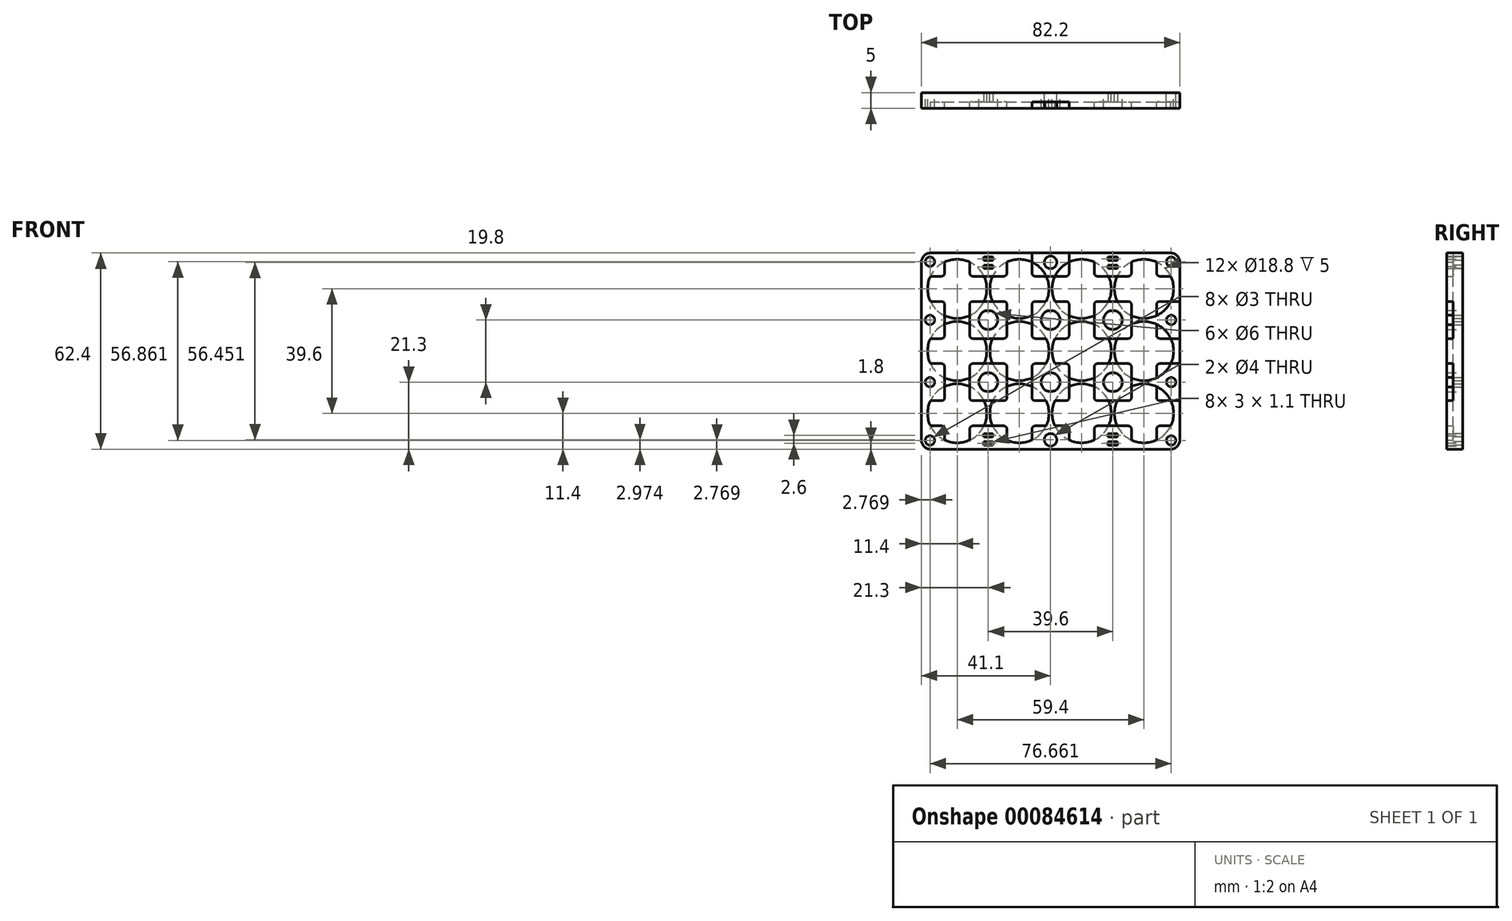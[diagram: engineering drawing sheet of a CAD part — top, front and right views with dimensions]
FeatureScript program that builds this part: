
annotation { "Feature Type Name" : "Feature", "Feature Type Description" : "" }
export const myFeature = defineFeature(function(context is Context, id is Id, definition is map)
    precondition{}
    {
        {
            var Q0;
            Q0=qCreatedBy(makeId("Front.planeOp"),FACE);
            var sketch = newSketch(context, id + "F0", { "sketchPlane" : qUnion([Q0]) });
            skCircle(sketch, "E0", {"center": v(0, 0) * mm, "radius": 9.4 * mm});
            skCircle(sketch, "E1.0.1.0", {"center": v(0, 19.8) * mm, "radius": 9.4 * mm});
            skCircle(sketch, "E1.0.2.0", {"center": v(0, 39.6) * mm, "radius": 9.4 * mm});
            skCircle(sketch, "E1.1.0.0", {"center": v(19.8, 0) * mm, "radius": 9.4 * mm});
            skCircle(sketch, "E1.1.1.0", {"center": v(19.8, 19.8) * mm, "radius": 9.4 * mm});
            skCircle(sketch, "E1.1.2.0", {"center": v(19.8, 39.6) * mm, "radius": 9.4 * mm});
            skCircle(sketch, "E1.2.0.0", {"center": v(39.6, 0) * mm, "radius": 9.4 * mm});
            skCircle(sketch, "E1.2.1.0", {"center": v(39.6, 19.8) * mm, "radius": 9.4 * mm});
            skCircle(sketch, "E1.2.2.0", {"center": v(39.6, 39.6) * mm, "radius": 9.4 * mm});
            skCircle(sketch, "E1.3.0.0", {"center": v(59.4, 0) * mm, "radius": 9.4 * mm});
            skCircle(sketch, "E1.3.1.0", {"center": v(59.4, 19.8) * mm, "radius": 9.4 * mm});
            skCircle(sketch, "E1.3.2.0", {"center": v(59.4, 39.6) * mm, "radius": 9.4 * mm});
            skLineSegment(sketch, "E1.direction1", {"start": v(0, 0) * mm, "end": v(19.8, 0) * mm, "construction": true});
            skLineSegment(sketch, "E1.direction2", {"start": v(0, 0) * mm, "end": v(0, 19.8) * mm, "construction": true});
            skLineSegment(sketch, "E2", {"start": v(-9.4, 19.8) * mm, "end": v(68.8, 19.8) * mm, "construction": true});
            skLineSegment(sketch, "E3", {"start": v(29.7, 19.8) * mm, "end": v(29.7, -16.3) * mm, "construction": true});
            skLineSegment(sketch, "E4.bottom", {"start": v(70.8, -11.4) * mm, "end": v(-11.4, -11.4) * mm});
            skLineSegment(sketch, "E4.top", {"start": v(70.8, 51) * mm, "end": v(-11.4, 51) * mm});
            skLineSegment(sketch, "E4.left", {"start": v(70.8, -11.4) * mm, "end": v(70.8, 51) * mm});
            skLineSegment(sketch, "E4.right", {"start": v(-11.4, -11.4) * mm, "end": v(-11.4, 51) * mm});
            skPoint(sketch, "E4.middle", {"position": v(29.7, 19.8) * mm});
            skLineSegment(sketch, "E5", {"start": v(19.8, 19.8) * mm, "end": v(0, 0) * mm, "construction": true});
            skLineSegment(sketch, "E6", {"start": v(19.8, 0) * mm, "end": v(0, 19.8) * mm, "construction": true});
            skCircle(sketch, "E7", {"center": v(9.9, 9.9) * mm, "radius": 3 * mm});
            skCircle(sketch, "E8.0.1.0", {"center": v(9.9, 29.7) * mm, "radius": 3 * mm});
            skCircle(sketch, "E8.1.0.0", {"center": v(29.7, 9.9) * mm, "radius": 3 * mm});
            skCircle(sketch, "E8.1.1.0", {"center": v(29.7, 29.7) * mm, "radius": 3 * mm});
            skCircle(sketch, "E8.2.0.0", {"center": v(49.5, 9.9) * mm, "radius": 3 * mm});
            skCircle(sketch, "E8.2.1.0", {"center": v(49.5, 29.7) * mm, "radius": 3 * mm});
            skLineSegment(sketch, "E8.direction1", {"start": v(9.9, 9.9) * mm, "end": v(29.7, 9.9) * mm, "construction": true});
            skLineSegment(sketch, "E8.direction2", {"start": v(9.9, 9.9) * mm, "end": v(9.9, 29.7) * mm, "construction": true});
            skLineSegment(sketch, "E9", {"start": v(9.9, 0) * mm, "end": v(9.9, -11.4) * mm, "construction": true});
            skCircle(sketch, "E10.1.0.0", {"center": v(29.7, -8.43) * mm, "radius": 2 * mm});
            skLineSegment(sketch, "E10.direction1", {"start": v(9.9, -8.43) * mm, "end": v(29.7, -8.43) * mm, "construction": true});
            skCircle(sketch, "E11.MirrorC", {"center": v(29.7, 48.03) * mm, "radius": 2 * mm});
            skLineSegment(sketch, "E12", {"start": v(0, 0) * mm, "end": v(-11.4, -11.4) * mm, "construction": true});
            skCircle(sketch, "E13", {"center": v(-8.63, -8.63) * mm, "radius": 1.5 * mm});
            skCircle(sketch, "E14", {"center": v(-8.63, 9.9) * mm, "radius": 1.5 * mm});
            skCircle(sketch, "E15", {"center": v(-8.63, 29.7) * mm, "radius": 1.5 * mm});
            skCircle(sketch, "E16.MirrorC", {"center": v(-8.63, 48.23) * mm, "radius": 1.5 * mm});
            skCircle(sketch, "E17.MirrorC", {"center": v(68.03, -8.63) * mm, "radius": 1.5 * mm});
            skCircle(sketch, "E18.MirrorC", {"center": v(68.03, 9.9) * mm, "radius": 1.5 * mm});
            skCircle(sketch, "E19.MirrorC", {"center": v(68.03, 29.7) * mm, "radius": 1.5 * mm});
            skCircle(sketch, "E20.MirrorC", {"center": v(68.03, 48.23) * mm, "radius": 1.5 * mm});
            skSolve(sketch);
        }
        {
            var Q0;
            Q0=qSketchRegion(id+"F0",true);
            extrude(context, id + "F1", {"entities" : qUnion([Q0]), "depth" : 3 * mm});
        }
        {
            var Q0;
            Q0=makeQuery(id+"F1.opExtrude","SWEPT_EDGE",EDGE,{"disambiguationData":[OSD([sQuery(id+"F0.wireOp",EDGE,"E4.top"),sQuery(id+"F0.wireOp",EDGE,"E4.left")])]});
            var Q1;
            Q1=makeQuery(id+"F1.opExtrude","SWEPT_EDGE",EDGE,{"disambiguationData":[OSD([sQuery(id+"F0.wireOp",EDGE,"E4.top"),sQuery(id+"F0.wireOp",EDGE,"E4.right")])]});
            var Q2;
            Q2=makeQuery(id+"F1.opExtrude","SWEPT_EDGE",EDGE,{"disambiguationData":[OSD([sQuery(id+"F0.wireOp",EDGE,"E4.bottom"),sQuery(id+"F0.wireOp",EDGE,"E4.right")])]});
            var Q3;
            Q3=makeQuery(id+"F1.opExtrude","SWEPT_EDGE",EDGE,{"disambiguationData":[OSD([sQuery(id+"F0.wireOp",EDGE,"E4.bottom"),sQuery(id+"F0.wireOp",EDGE,"E4.left")])]});
            fillet(context, id + "F2", {"entities" : qUnion([Q0, Q1, Q2, Q3]), "radius" : 3 * mm, "tangentPropagation" : true, "conicFillet" : false});
        }
        {
            var Q0;
            Q0=makeQuery(id+"F1.opExtrude","CAP_FACE",FACE,{"disambiguationData":[OSD([sQuery(id+"F0.wireOp",EDGE,"E0"),sQuery(id+"F0.wireOp",EDGE,"E1.0.1.0"),sQuery(id+"F0.wireOp",EDGE,"E1.0.2.0"),sQuery(id+"F0.wireOp",EDGE,"E1.1.0.0"),sQuery(id+"F0.wireOp",EDGE,"E1.1.1.0"),sQuery(id+"F0.wireOp",EDGE,"E1.1.2.0"),sQuery(id+"F0.wireOp",EDGE,"E1.2.0.0"),sQuery(id+"F0.wireOp",EDGE,"E1.2.1.0"),sQuery(id+"F0.wireOp",EDGE,"E1.2.2.0"),sQuery(id+"F0.wireOp",EDGE,"E1.3.0.0"),sQuery(id+"F0.wireOp",EDGE,"E1.3.1.0"),sQuery(id+"F0.wireOp",EDGE,"E1.3.2.0"),sQuery(id+"F0.wireOp",EDGE,"E4.bottom"),sQuery(id+"F0.wireOp",EDGE,"E4.top"),sQuery(id+"F0.wireOp",EDGE,"E4.left"),sQuery(id+"F0.wireOp",EDGE,"E4.right"),sQuery(id+"F0.wireOp",EDGE,"E7"),sQuery(id+"F0.wireOp",EDGE,"E8.0.1.0"),sQuery(id+"F0.wireOp",EDGE,"E8.1.0.0"),sQuery(id+"F0.wireOp",EDGE,"E8.1.1.0"),sQuery(id+"F0.wireOp",EDGE,"E8.2.0.0"),sQuery(id+"F0.wireOp",EDGE,"E8.2.1.0"),sQuery(id+"F0.wireOp",EDGE,"EQu0VpH5-7skk-RFPN-a941-U7lPeWaJFOTF"),sQuery(id+"F0.wireOp",EDGE,"E10.1.0.0"),sQuery(id+"F0.wireOp",EDGE,"E10.2.0.0"),sQuery(id+"F0.wireOp",EDGE,"d1583e0b-7ce3-4cbd-bf89-e67b3cb1275a0.MirrorC"),sQuery(id+"F0.wireOp",EDGE,"E11.MirrorC"),sQuery(id+"F0.wireOp",EDGE,"091dc890-a7a3-4dd7-b955-14caaaf945470.MirrorC"),sQuery(id+"F0.wireOp",EDGE,"E13"),sQuery(id+"F0.wireOp",EDGE,"E14"),sQuery(id+"F0.wireOp",EDGE,"E15"),sQuery(id+"F0.wireOp",EDGE,"E16.MirrorC"),sQuery(id+"F0.wireOp",EDGE,"E17.MirrorC"),sQuery(id+"F0.wireOp",EDGE,"E18.MirrorC"),sQuery(id+"F0.wireOp",EDGE,"E19.MirrorC"),sQuery(id+"F0.wireOp",EDGE,"E20.MirrorC")])],"isStart":false});
            var sketch = newSketch(context, id + "F3", { "sketchPlane" : qUnion([Q0]) });
            skLineSegment(sketch, "E21.0", {"start": v(67.8, 51) * mm, "end": v(-8.4, 51) * mm});
            skArc(sketch, "E21.1", {"start": v(-8.4, 51) * mm, "mid": v(-10.52, 50.12) * mm, "end": v(-11.4, 48) * mm});
            skLineSegment(sketch, "E21.2", {"start": v(-11.4, -8.4) * mm, "end": v(-11.4, 35.6) * mm});
            skArc(sketch, "E21.3", {"start": v(-11.4, -8.4) * mm, "mid": v(-10.52, -10.52) * mm, "end": v(-8.4, -11.4) * mm});
            skLineSegment(sketch, "E21.4", {"start": v(67.8, -11.4) * mm, "end": v(-8.4, -11.4) * mm});
            skArc(sketch, "E21.5", {"start": v(67.8, -11.4) * mm, "mid": v(69.92, -10.52) * mm, "end": v(70.8, -8.4) * mm});
            skLineSegment(sketch, "E21.6", {"start": v(70.8, -8.4) * mm, "end": v(70.8, 48) * mm});
            skArc(sketch, "E21.7", {"start": v(70.8, 48) * mm, "mid": v(69.92, 50.12) * mm, "end": v(67.8, 51) * mm});
            skCircle(sketch, "E21.8", {"center": v(59.4, 39.6) * mm, "radius": 9.4 * mm});
            skCircle(sketch, "E21.9", {"center": v(39.6, 39.6) * mm, "radius": 9.4 * mm});
            skCircle(sketch, "E21.10", {"center": v(19.8, 39.6) * mm, "radius": 9.4 * mm});
            skArc(sketch, "E21.11", {"start": v(-8.5, 43.6) * mm, "mid": v(-9.4, 39.6) * mm, "end": v(-8.5, 35.6) * mm});
            skCircle(sketch, "E21.12", {"center": v(0, 19.8) * mm, "radius": 9.4 * mm});
            skCircle(sketch, "E21.13", {"center": v(19.8, 19.8) * mm, "radius": 9.4 * mm});
            skCircle(sketch, "E21.14", {"center": v(39.6, 19.8) * mm, "radius": 9.4 * mm});
            skCircle(sketch, "E21.15", {"center": v(59.4, 19.8) * mm, "radius": 9.4 * mm});
            skCircle(sketch, "E21.16", {"center": v(59.4, 0) * mm, "radius": 9.4 * mm});
            skCircle(sketch, "E21.17", {"center": v(39.6, 0) * mm, "radius": 9.4 * mm});
            skCircle(sketch, "E21.18", {"center": v(19.8, 0) * mm, "radius": 9.4 * mm});
            skCircle(sketch, "E21.19", {"center": v(0, 0) * mm, "radius": 9.4 * mm});
            skLineSegment(sketch, "E22.left", {"start": v(-11.4, 39.6) * mm, "end": v(-11.4, 43.6) * mm});
            skLineSegment(sketch, "E22.right", {"start": v(70.8, 39.6) * mm, "end": v(70.8, 43.6) * mm});
            skLineSegment(sketch, "E23.trimOffspring", {"start": v(-11.4, 43.6) * mm, "end": v(-11.4, 48) * mm});
            skLineSegment(sketch, "E24", {"start": v(-4, 51) * mm, "end": v(-4, 43.6) * mm});
            skLineSegment(sketch, "E25.MirrorCS", {"start": v(4, 51) * mm, "end": v(4, 43.6) * mm});
            skLineSegment(sketch, "E26", {"start": v(-11.4, -4) * mm, "end": v(-4, -4) * mm});
            skLineSegment(sketch, "E27.MirrorCS", {"start": v(-11.4, 4) * mm, "end": v(-4, 4) * mm});
            skLineSegment(sketch, "E28.1.0.0", {"start": v(15.8, 51) * mm, "end": v(15.8, 43.6) * mm});
            skLineSegment(sketch, "E28.1.0.1", {"start": v(23.8, 51) * mm, "end": v(23.8, 43.6) * mm});
            skLineSegment(sketch, "E28.2.0.0", {"start": v(35.6, 51) * mm, "end": v(35.6, 43.6) * mm});
            skLineSegment(sketch, "E28.2.0.1", {"start": v(43.6, 51) * mm, "end": v(43.6, 43.6) * mm});
            skLineSegment(sketch, "E28.3.0.0", {"start": v(55.4, 51) * mm, "end": v(55.4, 43.6) * mm});
            skLineSegment(sketch, "E28.3.0.1", {"start": v(63.4, 51) * mm, "end": v(63.4, 43.6) * mm});
            skLineSegment(sketch, "E28.direction1", {"start": v(-4, -11.4) * mm, "end": v(15.8, -11.4) * mm, "construction": true});
            skLineSegment(sketch, "E29.0.1.0", {"start": v(-11.4, 23.8) * mm, "end": v(-4, 23.8) * mm});
            skLineSegment(sketch, "E29.0.1.1", {"start": v(-11.4, 15.8) * mm, "end": v(-4, 15.8) * mm});
            skLineSegment(sketch, "E29.0.2.0", {"start": v(-11.4, 43.6) * mm, "end": v(-4, 43.6) * mm});
            skLineSegment(sketch, "E29.0.2.1", {"start": v(-11.4, 35.6) * mm, "end": v(-4, 35.6) * mm});
            skLineSegment(sketch, "E29.direction1", {"start": v(-11.4, 4) * mm, "end": v(-4, 4) * mm, "construction": true});
            skLineSegment(sketch, "E29.direction2", {"start": v(-11.4, 4) * mm, "end": v(-11.4, 23.8) * mm, "construction": true});
            skLineSegment(sketch, "E30.trimOffspring", {"start": v(4, 35.6) * mm, "end": v(15.8, 35.6) * mm});
            skLineSegment(sketch, "E31.trimOffspring", {"start": v(4, 43.6) * mm, "end": v(15.8, 43.6) * mm});
            skLineSegment(sketch, "E32.trimOffspring", {"start": v(4, 35.6) * mm, "end": v(4, 23.8) * mm});
            skLineSegment(sketch, "E33.trimOffspring", {"start": v(-4, 35.6) * mm, "end": v(-4, 23.8) * mm});
            skLineSegment(sketch, "E34.trimOffspring", {"start": v(15.8, 35.6) * mm, "end": v(15.8, 23.8) * mm});
            skLineSegment(sketch, "E35.trimOffspring", {"start": v(23.8, 35.6) * mm, "end": v(23.8, 23.8) * mm});
            skLineSegment(sketch, "E36.trimOffspring", {"start": v(35.6, 35.6) * mm, "end": v(35.6, 23.8) * mm});
            skLineSegment(sketch, "E37.trimOffspring", {"start": v(43.6, 35.6) * mm, "end": v(43.6, 23.8) * mm});
            skLineSegment(sketch, "E38.trimOffspring", {"start": v(55.4, 35.6) * mm, "end": v(55.4, 23.8) * mm});
            skLineSegment(sketch, "E39.trimOffspring", {"start": v(63.4, 35.6) * mm, "end": v(63.4, 23.8) * mm});
            skLineSegment(sketch, "E40.trimOffspring", {"start": v(23.8, 43.6) * mm, "end": v(35.6, 43.6) * mm});
            skLineSegment(sketch, "E41.trimOffspring", {"start": v(43.6, 43.6) * mm, "end": v(55.4, 43.6) * mm});
            skLineSegment(sketch, "E42.trimOffspring", {"start": v(63.4, 43.6) * mm, "end": v(70.8, 43.6) * mm});
            skLineSegment(sketch, "E43.trimOffspring", {"start": v(63.4, 35.6) * mm, "end": v(70.8, 35.6) * mm});
            skLineSegment(sketch, "E44.trimOffspring", {"start": v(43.6, 35.6) * mm, "end": v(55.4, 35.6) * mm});
            skLineSegment(sketch, "E45.trimOffspring", {"start": v(23.8, 35.6) * mm, "end": v(35.6, 35.6) * mm});
            skLineSegment(sketch, "E46.trimOffspring", {"start": v(4, 23.8) * mm, "end": v(15.8, 23.8) * mm});
            skLineSegment(sketch, "E47.trimOffspring", {"start": v(4, 15.8) * mm, "end": v(11.3, 15.8) * mm});
            skLineSegment(sketch, "E48.trimOffspring", {"start": v(-4, 15.8) * mm, "end": v(-4, 4) * mm});
            skLineSegment(sketch, "E49.trimOffspring", {"start": v(4, 15.8) * mm, "end": v(4, 4) * mm});
            skLineSegment(sketch, "E50.trimOffspring", {"start": v(15.8, 15.8) * mm, "end": v(15.8, 4) * mm});
            skLineSegment(sketch, "E51.trimOffspring", {"start": v(23.8, 15.8) * mm, "end": v(23.8, 4) * mm});
            skLineSegment(sketch, "E52.trimOffspring", {"start": v(35.6, 15.8) * mm, "end": v(35.6, 4) * mm});
            skLineSegment(sketch, "E53.trimOffspring", {"start": v(43.6, 15.8) * mm, "end": v(43.6, 4) * mm});
            skLineSegment(sketch, "E54.trimOffspring", {"start": v(55.4, 15.8) * mm, "end": v(55.4, 4) * mm});
            skLineSegment(sketch, "E55.trimOffspring", {"start": v(63.4, 15.8) * mm, "end": v(63.4, 4) * mm});
            skLineSegment(sketch, "E56.trimOffspring", {"start": v(23.8, 23.8) * mm, "end": v(35.6, 23.8) * mm});
            skLineSegment(sketch, "E57.trimOffspring", {"start": v(43.6, 23.8) * mm, "end": v(55.4, 23.8) * mm});
            skLineSegment(sketch, "E58.trimOffspring", {"start": v(63.4, 23.8) * mm, "end": v(70.8, 23.8) * mm});
            skLineSegment(sketch, "E59.trimOffspring", {"start": v(23.8, 15.8) * mm, "end": v(35.6, 15.8) * mm});
            skLineSegment(sketch, "E60.trimOffspring", {"start": v(63.4, 15.8) * mm, "end": v(70.8, 15.8) * mm});
            skLineSegment(sketch, "E61.trimOffspring", {"start": v(63.4, 4) * mm, "end": v(70.8, 4) * mm});
            skLineSegment(sketch, "E62.trimOffspring", {"start": v(43.6, 4) * mm, "end": v(55.4, 4) * mm});
            skLineSegment(sketch, "E63.trimOffspring", {"start": v(23.8, 4) * mm, "end": v(35.6, 4) * mm});
            skLineSegment(sketch, "E64.trimOffspring", {"start": v(4, 4) * mm, "end": v(15.8, 4) * mm});
            skLineSegment(sketch, "E65.trimOffspring", {"start": v(4, -4) * mm, "end": v(11.3, -4) * mm});
            skLineSegment(sketch, "E66.trimOffspring", {"start": v(23.8, -4) * mm, "end": v(35.6, -4) * mm});
            skLineSegment(sketch, "E67.trimOffspring", {"start": v(63.4, -4) * mm, "end": v(70.8, -4) * mm});
            skLineSegment(sketch, "E68.trimOffspring", {"start": v(55.4, -4) * mm, "end": v(55.4, -11.4) * mm});
            skLineSegment(sketch, "E69.trimOffspring", {"start": v(63.4, -4) * mm, "end": v(63.4, -11.4) * mm});
            skLineSegment(sketch, "E70.trimOffspring", {"start": v(43.6, -4) * mm, "end": v(43.6, -11.4) * mm});
            skLineSegment(sketch, "E71.trimOffspring", {"start": v(35.6, -4) * mm, "end": v(35.6, -11.4) * mm});
            skLineSegment(sketch, "E72.trimOffspring", {"start": v(23.8, -4) * mm, "end": v(23.8, -11.4) * mm});
            skLineSegment(sketch, "E73.trimOffspring", {"start": v(4, -4) * mm, "end": v(4, -11.4) * mm});
            skLineSegment(sketch, "E74.trimOffspring", {"start": v(-4, -4) * mm, "end": v(-4, -11.4) * mm});
            skLineSegment(sketch, "E75", {"start": v(11.3, 15.8) * mm, "end": v(15.8, 15.8) * mm});
            skLineSegment(sketch, "E76", {"start": v(11.3, -4) * mm, "end": v(15.8, -4) * mm});
            skLineSegment(sketch, "E77.trimOffspring", {"start": v(15.8, -4) * mm, "end": v(15.8, -11.4) * mm});
            skLineSegment(sketch, "E78.trimOffspring", {"start": v(43.6, 15.8) * mm, "end": v(55.4, 15.8) * mm});
            skLineSegment(sketch, "E79.trimOffspring", {"start": v(4, 4) * mm, "end": v(13.6, 4) * mm, "construction": true});
            skLineSegment(sketch, "E80.trimOffspring", {"start": v(43.6, -4) * mm, "end": v(55.4, -4) * mm});
            skArc(sketch, "E81.trimOffspring", {"start": v(4, 48.1) * mm, "mid": v(0, 49) * mm, "end": v(-4, 48.1) * mm});
            skArc(sketch, "E82.trimOffspring", {"start": v(8.5, 35.6) * mm, "mid": v(9.4, 39.6) * mm, "end": v(8.5, 43.6) * mm});
            skArc(sketch, "E83.trimOffspring", {"start": v(-4, 31.1) * mm, "mid": v(0, 30.2) * mm, "end": v(4, 31.1) * mm});
            skSolve(sketch);
        }
        {
            var Q0;
            {var subQ6=sQuery(id+"F3.wireOp",EDGE,"E21.1");Q0=makeQuery(id+"F3.imprint","IMPRINT",FACE,{"disambiguationData":[TD([[makeQuery(id+"F3.imprint","IMPRINT",EDGE,{"derivedFrom":subQ6}),1.0]])]});}
            var Q1;
            {var subQ0=sQuery(id+"F3.wireOp",EDGE,"E29.0.2.0");var subQ1=sQuery(id+"F3.wireOp",EDGE,"E24");var subQ2=makeQuery(id+"F3.imprint","INTERSECT",VERTEX,{"derivedFrom":[subQ1,subQ0]});Q1=makeQuery(id+"F3.imprint","IMPRINT",FACE,{"disambiguationData":[TD([[makeQuery(id+"F3.imprint","IMPRINT",EDGE,{"disambiguationData":[TD([[subQ2,1.0]])],"derivedFrom":subQ1}),-1.0]])]});}
            var Q2;
            {var subQ0=sQuery(id+"F3.wireOp",EDGE,"E31.trimOffspring");var subQ1=sQuery(id+"F3.wireOp",EDGE,"E25.MirrorCS");var subQ2=makeQuery(id+"F3.imprint","INTERSECT",VERTEX,{"derivedFrom":[subQ1,subQ0]});Q2=makeQuery(id+"F3.imprint","IMPRINT",FACE,{"disambiguationData":[TD([[makeQuery(id+"F3.imprint","IMPRINT",EDGE,{"disambiguationData":[TD([[subQ2,1.0]])],"derivedFrom":subQ1}),1.0]])]});}
            var Q3;
            Q3=makeQuery(id+"F3.imprint","IMPRINT",FACE,{"disambiguationData":[TD([[makeQuery(id+"F3.imprint","IMPRINT",EDGE,{"derivedFrom":makeQuery(id+"F1.opExtrude","CAP_EDGE",EDGE,{"disambiguationData":[OSD([sQuery(id+"F0.wireOp",EDGE,"d1583e0b-7ce3-4cbd-bf89-e67b3cb1275a0.MirrorC")])],"isStart":false})}),1.0]])]});
            var Q4;
            {var subQ0=sQuery(id+"F3.wireOp",EDGE,"E31.trimOffspring");var subQ1=sQuery(id+"F3.wireOp",EDGE,"E28.1.0.0");var subQ2=makeQuery(id+"F3.imprint","INTERSECT",VERTEX,{"derivedFrom":[subQ1,subQ0]});Q4=makeQuery(id+"F3.imprint","IMPRINT",FACE,{"disambiguationData":[TD([[makeQuery(id+"F3.imprint","IMPRINT",EDGE,{"disambiguationData":[TD([[subQ2,1.0]])],"derivedFrom":subQ1}),-1.0]])]});}
            var Q5;
            {var subQ0=sQuery(id+"F3.wireOp",EDGE,"E40.trimOffspring");var subQ1=sQuery(id+"F3.wireOp",EDGE,"E28.1.0.1");var subQ2=makeQuery(id+"F3.imprint","INTERSECT",VERTEX,{"derivedFrom":[subQ1,subQ0]});Q5=makeQuery(id+"F3.imprint","IMPRINT",FACE,{"disambiguationData":[TD([[makeQuery(id+"F3.imprint","IMPRINT",EDGE,{"disambiguationData":[TD([[subQ2,1.0]])],"derivedFrom":subQ1}),1.0]])]});}
            var Q6;
            Q6=makeQuery(id+"F3.imprint","IMPRINT",FACE,{"disambiguationData":[TD([[makeQuery(id+"F3.imprint","IMPRINT",EDGE,{"derivedFrom":makeQuery(id+"F1.opExtrude","CAP_EDGE",EDGE,{"disambiguationData":[OSD([sQuery(id+"F0.wireOp",EDGE,"E11.MirrorC")])],"isStart":false})}),1.0]])]});
            var Q7;
            {var subQ0=sQuery(id+"F3.wireOp",EDGE,"E28.2.0.0");var subQ1=sQuery(id+"F3.wireOp",EDGE,"E21.9");var subQ2=makeQuery(id+"F3.imprint","INTERSECT",VERTEX,{"derivedFrom":[subQ1,subQ0]});Q7=makeQuery(id+"F3.imprint","IMPRINT",FACE,{"disambiguationData":[TD([[makeQuery(id+"F3.imprint","IMPRINT",EDGE,{"disambiguationData":[TD([[subQ2,-1.0]])],"derivedFrom":subQ1}),1.0]])]});}
            var Q8;
            {var subQ0=sQuery(id+"F3.wireOp",EDGE,"E28.2.0.1");var subQ1=sQuery(id+"F3.wireOp",EDGE,"E21.9");var subQ2=makeQuery(id+"F3.imprint","INTERSECT",VERTEX,{"derivedFrom":[subQ1,subQ0]});Q8=makeQuery(id+"F3.imprint","IMPRINT",FACE,{"disambiguationData":[TD([[makeQuery(id+"F3.imprint","IMPRINT",EDGE,{"disambiguationData":[TD([[subQ2,1.0]])],"derivedFrom":subQ1}),1.0]])]});}
            var Q9;
            Q9=makeQuery(id+"F3.imprint","IMPRINT",FACE,{"disambiguationData":[TD([[makeQuery(id+"F3.imprint","IMPRINT",EDGE,{"derivedFrom":makeQuery(id+"F1.opExtrude","CAP_EDGE",EDGE,{"disambiguationData":[OSD([sQuery(id+"F0.wireOp",EDGE,"091dc890-a7a3-4dd7-b955-14caaaf945470.MirrorC")])],"isStart":false})}),1.0]])]});
            var Q10;
            {var subQ0=sQuery(id+"F3.wireOp",EDGE,"E41.trimOffspring");var subQ1=sQuery(id+"F3.wireOp",EDGE,"E28.3.0.0");var subQ2=makeQuery(id+"F3.imprint","INTERSECT",VERTEX,{"derivedFrom":[subQ1,subQ0]});Q10=makeQuery(id+"F3.imprint","IMPRINT",FACE,{"disambiguationData":[TD([[makeQuery(id+"F3.imprint","IMPRINT",EDGE,{"disambiguationData":[TD([[subQ2,1.0]])],"derivedFrom":subQ1}),-1.0]])]});}
            var Q11;
            {var subQ0=sQuery(id+"F3.wireOp",EDGE,"E42.trimOffspring");var subQ1=sQuery(id+"F3.wireOp",EDGE,"E28.3.0.1");var subQ2=makeQuery(id+"F3.imprint","INTERSECT",VERTEX,{"derivedFrom":[subQ1,subQ0]});Q11=makeQuery(id+"F3.imprint","IMPRINT",FACE,{"disambiguationData":[TD([[makeQuery(id+"F3.imprint","IMPRINT",EDGE,{"disambiguationData":[TD([[subQ2,1.0]])],"derivedFrom":subQ1}),1.0]])]});}
            var Q12;
            {var subQ9=sQuery(id+"F3.wireOp",EDGE,"E21.7");Q12=makeQuery(id+"F3.imprint","IMPRINT",FACE,{"disambiguationData":[TD([[makeQuery(id+"F3.imprint","IMPRINT",EDGE,{"derivedFrom":subQ9}),1.0]])]});}
            var Q13;
            {var subQ0=sQuery(id+"F3.wireOp",EDGE,"E58.trimOffspring");var subQ1=sQuery(id+"F3.wireOp",EDGE,"E39.trimOffspring");var subQ2=makeQuery(id+"F3.imprint","INTERSECT",VERTEX,{"derivedFrom":[subQ1,subQ0]});Q13=makeQuery(id+"F3.imprint","IMPRINT",FACE,{"disambiguationData":[TD([[makeQuery(id+"F3.imprint","IMPRINT",EDGE,{"disambiguationData":[TD([[subQ2,1.0]])],"derivedFrom":subQ1}),1.0]])]});}
            var Q14;
            Q14=makeQuery(id+"F3.imprint","IMPRINT",FACE,{"disambiguationData":[TD([[makeQuery(id+"F3.imprint","IMPRINT",EDGE,{"derivedFrom":makeQuery(id+"F1.opExtrude","CAP_EDGE",EDGE,{"disambiguationData":[OSD([sQuery(id+"F0.wireOp",EDGE,"E19.MirrorC")])],"isStart":false})}),1.0]])]});
            var Q15;
            {var subQ0=sQuery(id+"F3.wireOp",EDGE,"E43.trimOffspring");var subQ1=sQuery(id+"F3.wireOp",EDGE,"E39.trimOffspring");var subQ2=makeQuery(id+"F3.imprint","INTERSECT",VERTEX,{"derivedFrom":[subQ1,subQ0]});Q15=makeQuery(id+"F3.imprint","IMPRINT",FACE,{"disambiguationData":[TD([[makeQuery(id+"F3.imprint","IMPRINT",EDGE,{"disambiguationData":[TD([[subQ2,-1.0]])],"derivedFrom":subQ1}),1.0]])]});}
            var Q16;
            {var subQ0=sQuery(id+"F3.wireOp",EDGE,"E57.trimOffspring");var subQ1=sQuery(id+"F3.wireOp",EDGE,"E38.trimOffspring");var subQ2=makeQuery(id+"F3.imprint","INTERSECT",VERTEX,{"derivedFrom":[subQ1,subQ0]});Q16=makeQuery(id+"F3.imprint","IMPRINT",FACE,{"disambiguationData":[TD([[makeQuery(id+"F3.imprint","IMPRINT",EDGE,{"disambiguationData":[TD([[subQ2,1.0]])],"derivedFrom":subQ1}),-1.0]])]});}
            var Q17;
            {var subQ0=sQuery(id+"F3.wireOp",EDGE,"E57.trimOffspring");var subQ1=sQuery(id+"F3.wireOp",EDGE,"E37.trimOffspring");var subQ2=makeQuery(id+"F3.imprint","INTERSECT",VERTEX,{"derivedFrom":[subQ1,subQ0]});Q17=makeQuery(id+"F3.imprint","IMPRINT",FACE,{"disambiguationData":[TD([[makeQuery(id+"F3.imprint","IMPRINT",EDGE,{"disambiguationData":[TD([[subQ2,1.0]])],"derivedFrom":subQ1}),1.0]])]});}
            var Q18;
            {var subQ0=sQuery(id+"F3.wireOp",EDGE,"E37.trimOffspring");var subQ1=sQuery(id+"F3.wireOp",EDGE,"E21.9");var subQ2=makeQuery(id+"F3.imprint","INTERSECT",VERTEX,{"derivedFrom":[subQ1,subQ0]});Q18=makeQuery(id+"F3.imprint","IMPRINT",FACE,{"disambiguationData":[TD([[makeQuery(id+"F3.imprint","IMPRINT",EDGE,{"disambiguationData":[TD([[subQ2,-1.0]])],"derivedFrom":subQ1}),1.0]])]});}
            var Q19;
            {var subQ0=sQuery(id+"F3.wireOp",EDGE,"E44.trimOffspring");var subQ1=sQuery(id+"F3.wireOp",EDGE,"E38.trimOffspring");var subQ2=makeQuery(id+"F3.imprint","INTERSECT",VERTEX,{"derivedFrom":[subQ1,subQ0]});Q19=makeQuery(id+"F3.imprint","IMPRINT",FACE,{"disambiguationData":[TD([[makeQuery(id+"F3.imprint","IMPRINT",EDGE,{"disambiguationData":[TD([[subQ2,-1.0]])],"derivedFrom":subQ1}),-1.0]])]});}
            var Q20;
            Q20=makeQuery(id+"F3.imprint","IMPRINT",FACE,{"disambiguationData":[TD([[makeQuery(id+"F3.imprint","IMPRINT",EDGE,{"derivedFrom":makeQuery(id+"F1.opExtrude","CAP_EDGE",EDGE,{"disambiguationData":[OSD([sQuery(id+"F0.wireOp",EDGE,"E8.2.1.0")])],"isStart":false})}),-1.0]])]});
            var Q21;
            {var subQ0=sQuery(id+"F3.wireOp",EDGE,"E45.trimOffspring");var subQ1=sQuery(id+"F3.wireOp",EDGE,"E35.trimOffspring");var subQ2=makeQuery(id+"F3.imprint","INTERSECT",VERTEX,{"derivedFrom":[subQ1,subQ0]});Q21=makeQuery(id+"F3.imprint","IMPRINT",FACE,{"disambiguationData":[TD([[makeQuery(id+"F3.imprint","IMPRINT",EDGE,{"disambiguationData":[TD([[subQ2,-1.0]])],"derivedFrom":subQ1}),1.0]])]});}
            var Q22;
            {var subQ0=sQuery(id+"F3.wireOp",EDGE,"E56.trimOffspring");var subQ1=sQuery(id+"F3.wireOp",EDGE,"E35.trimOffspring");var subQ2=makeQuery(id+"F3.imprint","INTERSECT",VERTEX,{"derivedFrom":[subQ1,subQ0]});Q22=makeQuery(id+"F3.imprint","IMPRINT",FACE,{"disambiguationData":[TD([[makeQuery(id+"F3.imprint","IMPRINT",EDGE,{"disambiguationData":[TD([[subQ2,1.0]])],"derivedFrom":subQ1}),1.0]])]});}
            var Q23;
            {var subQ0=sQuery(id+"F3.wireOp",EDGE,"E56.trimOffspring");var subQ1=sQuery(id+"F3.wireOp",EDGE,"E36.trimOffspring");var subQ2=makeQuery(id+"F3.imprint","INTERSECT",VERTEX,{"derivedFrom":[subQ1,subQ0]});Q23=makeQuery(id+"F3.imprint","IMPRINT",FACE,{"disambiguationData":[TD([[makeQuery(id+"F3.imprint","IMPRINT",EDGE,{"disambiguationData":[TD([[subQ2,1.0]])],"derivedFrom":subQ1}),-1.0]])]});}
            var Q24;
            {var subQ0=sQuery(id+"F3.wireOp",EDGE,"E45.trimOffspring");var subQ1=sQuery(id+"F3.wireOp",EDGE,"E21.9");var subQ2=makeQuery(id+"F3.imprint","INTERSECT",VERTEX,{"derivedFrom":[subQ1,subQ0]});Q24=makeQuery(id+"F3.imprint","IMPRINT",FACE,{"disambiguationData":[TD([[makeQuery(id+"F3.imprint","IMPRINT",EDGE,{"disambiguationData":[TD([[subQ2,-1.0]])],"derivedFrom":subQ1}),1.0]])]});}
            var Q25;
            Q25=makeQuery(id+"F3.imprint","IMPRINT",FACE,{"disambiguationData":[TD([[makeQuery(id+"F3.imprint","IMPRINT",EDGE,{"derivedFrom":makeQuery(id+"F1.opExtrude","CAP_EDGE",EDGE,{"disambiguationData":[OSD([sQuery(id+"F0.wireOp",EDGE,"E8.1.1.0")])],"isStart":false})}),-1.0]])]});
            var Q26;
            Q26=makeQuery(id+"F3.imprint","IMPRINT",FACE,{"disambiguationData":[TD([[makeQuery(id+"F3.imprint","IMPRINT",EDGE,{"derivedFrom":makeQuery(id+"F1.opExtrude","CAP_EDGE",EDGE,{"disambiguationData":[OSD([sQuery(id+"F0.wireOp",EDGE,"E8.0.1.0")])],"isStart":false})}),-1.0]])]});
            var Q27;
            {var subQ0=sQuery(id+"F3.wireOp",EDGE,"E32.trimOffspring");var subQ1=sQuery(id+"F3.wireOp",EDGE,"E30.trimOffspring");var subQ2=makeQuery(id+"F3.imprint","INTERSECT",VERTEX,{"derivedFrom":[subQ1,subQ0]});Q27=makeQuery(id+"F3.imprint","IMPRINT",FACE,{"disambiguationData":[TD([[makeQuery(id+"F3.imprint","IMPRINT",EDGE,{"disambiguationData":[TD([[subQ2,-1.0]])],"derivedFrom":subQ1}),-1.0]])]});}
            var Q28;
            {var subQ0=sQuery(id+"F3.wireOp",EDGE,"E34.trimOffspring");var subQ1=sQuery(id+"F3.wireOp",EDGE,"E30.trimOffspring");var subQ2=makeQuery(id+"F3.imprint","INTERSECT",VERTEX,{"derivedFrom":[subQ1,subQ0]});Q28=makeQuery(id+"F3.imprint","IMPRINT",FACE,{"disambiguationData":[TD([[makeQuery(id+"F3.imprint","IMPRINT",EDGE,{"disambiguationData":[TD([[subQ2,1.0]])],"derivedFrom":subQ1}),-1.0]])]});}
            var Q29;
            {var subQ0=sQuery(id+"F3.wireOp",EDGE,"E46.trimOffspring");var subQ1=sQuery(id+"F3.wireOp",EDGE,"E34.trimOffspring");var subQ2=makeQuery(id+"F3.imprint","INTERSECT",VERTEX,{"derivedFrom":[subQ1,subQ0]});Q29=makeQuery(id+"F3.imprint","IMPRINT",FACE,{"disambiguationData":[TD([[makeQuery(id+"F3.imprint","IMPRINT",EDGE,{"disambiguationData":[TD([[subQ2,1.0]])],"derivedFrom":subQ1}),-1.0]])]});}
            var Q30;
            {var subQ0=sQuery(id+"F3.wireOp",EDGE,"E46.trimOffspring");var subQ1=sQuery(id+"F3.wireOp",EDGE,"E32.trimOffspring");var subQ2=makeQuery(id+"F3.imprint","INTERSECT",VERTEX,{"derivedFrom":[subQ1,subQ0]});Q30=makeQuery(id+"F3.imprint","IMPRINT",FACE,{"disambiguationData":[TD([[makeQuery(id+"F3.imprint","IMPRINT",EDGE,{"disambiguationData":[TD([[subQ2,1.0]])],"derivedFrom":subQ1}),1.0]])]});}
            var Q31;
            Q31=makeQuery(id+"F3.imprint","IMPRINT",FACE,{"disambiguationData":[TD([[makeQuery(id+"F3.imprint","IMPRINT",EDGE,{"derivedFrom":makeQuery(id+"F1.opExtrude","CAP_EDGE",EDGE,{"disambiguationData":[OSD([sQuery(id+"F0.wireOp",EDGE,"E14")])],"isStart":false})}),-1.0]])]});
            var Q32;
            {var subQ0=sQuery(id+"F3.wireOp",EDGE,"E48.trimOffspring");var subQ1=sQuery(id+"F3.wireOp",EDGE,"E29.0.1.1");var subQ2=makeQuery(id+"F3.imprint","INTERSECT",VERTEX,{"derivedFrom":[subQ1,subQ0]});Q32=makeQuery(id+"F3.imprint","IMPRINT",FACE,{"disambiguationData":[TD([[makeQuery(id+"F3.imprint","IMPRINT",EDGE,{"disambiguationData":[TD([[subQ2,1.0]])],"derivedFrom":subQ1}),-1.0]])]});}
            var Q33;
            {var subQ0=sQuery(id+"F3.wireOp",EDGE,"E48.trimOffspring");var subQ1=sQuery(id+"F3.wireOp",EDGE,"E27.MirrorCS");var subQ2=makeQuery(id+"F3.imprint","INTERSECT",VERTEX,{"derivedFrom":[subQ1,subQ0]});Q33=makeQuery(id+"F3.imprint","IMPRINT",FACE,{"disambiguationData":[TD([[makeQuery(id+"F3.imprint","IMPRINT",EDGE,{"disambiguationData":[TD([[subQ2,1.0]])],"derivedFrom":subQ1}),1.0]])]});}
            var Q34;
            {var subQ1=sQuery(id+"F3.wireOp",EDGE,"E21.3");Q34=makeQuery(id+"F3.imprint","IMPRINT",FACE,{"disambiguationData":[TD([[makeQuery(id+"F3.imprint","IMPRINT",EDGE,{"derivedFrom":subQ1}),1.0]])]});}
            var Q35;
            {var subQ0=sQuery(id+"F3.wireOp",EDGE,"E74.trimOffspring");var subQ1=sQuery(id+"F3.wireOp",EDGE,"E26");var subQ2=makeQuery(id+"F3.imprint","INTERSECT",VERTEX,{"derivedFrom":[subQ1,subQ0]});Q35=makeQuery(id+"F3.imprint","IMPRINT",FACE,{"disambiguationData":[TD([[makeQuery(id+"F3.imprint","IMPRINT",EDGE,{"disambiguationData":[TD([[subQ2,1.0]])],"derivedFrom":subQ1}),-1.0]])]});}
            var Q36;
            Q36=makeQuery(id+"F3.imprint","IMPRINT",FACE,{"disambiguationData":[TD([[makeQuery(id+"F3.imprint","IMPRINT",EDGE,{"derivedFrom":makeQuery(id+"F1.opExtrude","CAP_EDGE",EDGE,{"disambiguationData":[OSD([sQuery(id+"F0.wireOp",EDGE,"EQu0VpH5-7skk-RFPN-a941-U7lPeWaJFOTF")])],"isStart":false})}),-1.0]])]});
            var Q37;
            {var subQ0=sQuery(id+"F3.wireOp",EDGE,"E73.trimOffspring");var subQ1=sQuery(id+"F3.wireOp",EDGE,"E65.trimOffspring");var subQ2=makeQuery(id+"F3.imprint","INTERSECT",VERTEX,{"derivedFrom":[subQ1,subQ0]});Q37=makeQuery(id+"F3.imprint","IMPRINT",FACE,{"disambiguationData":[TD([[makeQuery(id+"F3.imprint","IMPRINT",EDGE,{"disambiguationData":[TD([[subQ2,-1.0]])],"derivedFrom":subQ1}),-1.0]])]});}
            var Q38;
            {var subQ0=sQuery(id+"F3.wireOp",EDGE,"E76");Q38=makeQuery(id+"F3.imprint","IMPRINT",FACE,{"disambiguationData":[TD([[makeQuery(id+"F3.imprint","IMPRINT",EDGE,{"derivedFrom":subQ0}),-1.0]])]});}
            var Q39;
            Q39=makeQuery(id+"F3.imprint","IMPRINT",FACE,{"disambiguationData":[TD([[makeQuery(id+"F3.imprint","IMPRINT",EDGE,{"derivedFrom":makeQuery(id+"F1.opExtrude","CAP_EDGE",EDGE,{"disambiguationData":[OSD([sQuery(id+"F0.wireOp",EDGE,"E10.1.0.0")])],"isStart":false})}),-1.0]])]});
            var Q40;
            {var subQ0=sQuery(id+"F3.wireOp",EDGE,"E72.trimOffspring");var subQ1=sQuery(id+"F3.wireOp",EDGE,"E66.trimOffspring");var subQ2=makeQuery(id+"F3.imprint","INTERSECT",VERTEX,{"derivedFrom":[subQ1,subQ0]});Q40=makeQuery(id+"F3.imprint","IMPRINT",FACE,{"disambiguationData":[TD([[makeQuery(id+"F3.imprint","IMPRINT",EDGE,{"disambiguationData":[TD([[subQ2,-1.0]])],"derivedFrom":subQ1}),-1.0]])]});}
            var Q41;
            {var subQ0=sQuery(id+"F3.wireOp",EDGE,"E71.trimOffspring");var subQ1=sQuery(id+"F3.wireOp",EDGE,"E66.trimOffspring");var subQ2=makeQuery(id+"F3.imprint","INTERSECT",VERTEX,{"derivedFrom":[subQ1,subQ0]});Q41=makeQuery(id+"F3.imprint","IMPRINT",FACE,{"disambiguationData":[TD([[makeQuery(id+"F3.imprint","IMPRINT",EDGE,{"disambiguationData":[TD([[subQ2,1.0]])],"derivedFrom":subQ1}),-1.0]])]});}
            var Q42;
            Q42=makeQuery(id+"F3.imprint","IMPRINT",FACE,{"disambiguationData":[TD([[makeQuery(id+"F3.imprint","IMPRINT",EDGE,{"derivedFrom":makeQuery(id+"F1.opExtrude","CAP_EDGE",EDGE,{"disambiguationData":[OSD([sQuery(id+"F0.wireOp",EDGE,"E10.2.0.0")])],"isStart":false})}),-1.0]])]});
            var Q43;
            {var subQ0=sQuery(id+"F3.wireOp",EDGE,"E80.trimOffspring");var subQ1=sQuery(id+"F3.wireOp",EDGE,"E70.trimOffspring");var subQ2=makeQuery(id+"F3.imprint","INTERSECT",VERTEX,{"derivedFrom":[subQ1,subQ0]});Q43=makeQuery(id+"F3.imprint","IMPRINT",FACE,{"disambiguationData":[TD([[makeQuery(id+"F3.imprint","IMPRINT",EDGE,{"disambiguationData":[TD([[subQ2,-1.0]])],"derivedFrom":subQ1}),1.0]])]});}
            var Q44;
            {var subQ0=sQuery(id+"F3.wireOp",EDGE,"E80.trimOffspring");var subQ1=sQuery(id+"F3.wireOp",EDGE,"E68.trimOffspring");var subQ2=makeQuery(id+"F3.imprint","INTERSECT",VERTEX,{"derivedFrom":[subQ1,subQ0]});Q44=makeQuery(id+"F3.imprint","IMPRINT",FACE,{"disambiguationData":[TD([[makeQuery(id+"F3.imprint","IMPRINT",EDGE,{"disambiguationData":[TD([[subQ2,-1.0]])],"derivedFrom":subQ1}),-1.0]])]});}
            var Q45;
            {var subQ0=sQuery(id+"F3.wireOp",EDGE,"E69.trimOffspring");var subQ1=sQuery(id+"F3.wireOp",EDGE,"E67.trimOffspring");var subQ2=makeQuery(id+"F3.imprint","INTERSECT",VERTEX,{"derivedFrom":[subQ1,subQ0]});Q45=makeQuery(id+"F3.imprint","IMPRINT",FACE,{"disambiguationData":[TD([[makeQuery(id+"F3.imprint","IMPRINT",EDGE,{"disambiguationData":[TD([[subQ2,-1.0]])],"derivedFrom":subQ1}),-1.0]])]});}
            var Q46;
            {var subQ1=sQuery(id+"F3.wireOp",EDGE,"E21.5");Q46=makeQuery(id+"F3.imprint","IMPRINT",FACE,{"disambiguationData":[TD([[makeQuery(id+"F3.imprint","IMPRINT",EDGE,{"derivedFrom":subQ1}),1.0]])]});}
            var Q47;
            Q47=makeQuery(id+"F3.imprint","IMPRINT",FACE,{"disambiguationData":[TD([[makeQuery(id+"F3.imprint","IMPRINT",EDGE,{"derivedFrom":makeQuery(id+"F1.opExtrude","CAP_EDGE",EDGE,{"disambiguationData":[OSD([sQuery(id+"F0.wireOp",EDGE,"E18.MirrorC")])],"isStart":false})}),1.0]])]});
            var Q48;
            {var subQ0=sQuery(id+"F3.wireOp",EDGE,"E61.trimOffspring");var subQ1=sQuery(id+"F3.wireOp",EDGE,"E55.trimOffspring");var subQ2=makeQuery(id+"F3.imprint","INTERSECT",VERTEX,{"derivedFrom":[subQ1,subQ0]});Q48=makeQuery(id+"F3.imprint","IMPRINT",FACE,{"disambiguationData":[TD([[makeQuery(id+"F3.imprint","IMPRINT",EDGE,{"disambiguationData":[TD([[subQ2,1.0]])],"derivedFrom":subQ1}),1.0]])]});}
            var Q49;
            {var subQ0=sQuery(id+"F3.wireOp",EDGE,"E60.trimOffspring");var subQ1=sQuery(id+"F3.wireOp",EDGE,"E55.trimOffspring");var subQ2=makeQuery(id+"F3.imprint","INTERSECT",VERTEX,{"derivedFrom":[subQ1,subQ0]});Q49=makeQuery(id+"F3.imprint","IMPRINT",FACE,{"disambiguationData":[TD([[makeQuery(id+"F3.imprint","IMPRINT",EDGE,{"disambiguationData":[TD([[subQ2,-1.0]])],"derivedFrom":subQ1}),1.0]])]});}
            var Q50;
            {var subQ0=sQuery(id+"F3.wireOp",EDGE,"E62.trimOffspring");var subQ1=sQuery(id+"F3.wireOp",EDGE,"E54.trimOffspring");var subQ2=makeQuery(id+"F3.imprint","INTERSECT",VERTEX,{"derivedFrom":[subQ1,subQ0]});Q50=makeQuery(id+"F3.imprint","IMPRINT",FACE,{"disambiguationData":[TD([[makeQuery(id+"F3.imprint","IMPRINT",EDGE,{"disambiguationData":[TD([[subQ2,1.0]])],"derivedFrom":subQ1}),-1.0]])]});}
            var Q51;
            {var subQ0=sQuery(id+"F3.wireOp",EDGE,"E62.trimOffspring");var subQ1=sQuery(id+"F3.wireOp",EDGE,"E53.trimOffspring");var subQ2=makeQuery(id+"F3.imprint","INTERSECT",VERTEX,{"derivedFrom":[subQ1,subQ0]});Q51=makeQuery(id+"F3.imprint","IMPRINT",FACE,{"disambiguationData":[TD([[makeQuery(id+"F3.imprint","IMPRINT",EDGE,{"disambiguationData":[TD([[subQ2,1.0]])],"derivedFrom":subQ1}),1.0]])]});}
            var Q52;
            Q52=makeQuery(id+"F3.imprint","IMPRINT",FACE,{"disambiguationData":[TD([[makeQuery(id+"F3.imprint","IMPRINT",EDGE,{"derivedFrom":makeQuery(id+"F1.opExtrude","CAP_EDGE",EDGE,{"disambiguationData":[OSD([sQuery(id+"F0.wireOp",EDGE,"E8.2.0.0")])],"isStart":false})}),-1.0]])]});
            var Q53;
            {var subQ0=sQuery(id+"F3.wireOp",EDGE,"E78.trimOffspring");var subQ1=sQuery(id+"F3.wireOp",EDGE,"E53.trimOffspring");var subQ2=makeQuery(id+"F3.imprint","INTERSECT",VERTEX,{"derivedFrom":[subQ1,subQ0]});Q53=makeQuery(id+"F3.imprint","IMPRINT",FACE,{"disambiguationData":[TD([[makeQuery(id+"F3.imprint","IMPRINT",EDGE,{"disambiguationData":[TD([[subQ2,-1.0]])],"derivedFrom":subQ1}),1.0]])]});}
            var Q54;
            {var subQ0=sQuery(id+"F3.wireOp",EDGE,"E78.trimOffspring");var subQ1=sQuery(id+"F3.wireOp",EDGE,"E54.trimOffspring");var subQ2=makeQuery(id+"F3.imprint","INTERSECT",VERTEX,{"derivedFrom":[subQ1,subQ0]});Q54=makeQuery(id+"F3.imprint","IMPRINT",FACE,{"disambiguationData":[TD([[makeQuery(id+"F3.imprint","IMPRINT",EDGE,{"disambiguationData":[TD([[subQ2,-1.0]])],"derivedFrom":subQ1}),-1.0]])]});}
            var Q55;
            {var subQ0=sQuery(id+"F3.wireOp",EDGE,"E63.trimOffspring");var subQ1=sQuery(id+"F3.wireOp",EDGE,"E52.trimOffspring");var subQ2=makeQuery(id+"F3.imprint","INTERSECT",VERTEX,{"derivedFrom":[subQ1,subQ0]});Q55=makeQuery(id+"F3.imprint","IMPRINT",FACE,{"disambiguationData":[TD([[makeQuery(id+"F3.imprint","IMPRINT",EDGE,{"disambiguationData":[TD([[subQ2,1.0]])],"derivedFrom":subQ1}),-1.0]])]});}
            var Q56;
            {var subQ0=sQuery(id+"F3.wireOp",EDGE,"E63.trimOffspring");var subQ1=sQuery(id+"F3.wireOp",EDGE,"E51.trimOffspring");var subQ2=makeQuery(id+"F3.imprint","INTERSECT",VERTEX,{"derivedFrom":[subQ1,subQ0]});Q56=makeQuery(id+"F3.imprint","IMPRINT",FACE,{"disambiguationData":[TD([[makeQuery(id+"F3.imprint","IMPRINT",EDGE,{"disambiguationData":[TD([[subQ2,1.0]])],"derivedFrom":subQ1}),1.0]])]});}
            var Q57;
            {var subQ0=sQuery(id+"F3.wireOp",EDGE,"E59.trimOffspring");var subQ1=sQuery(id+"F3.wireOp",EDGE,"E51.trimOffspring");var subQ2=makeQuery(id+"F3.imprint","INTERSECT",VERTEX,{"derivedFrom":[subQ1,subQ0]});Q57=makeQuery(id+"F3.imprint","IMPRINT",FACE,{"disambiguationData":[TD([[makeQuery(id+"F3.imprint","IMPRINT",EDGE,{"disambiguationData":[TD([[subQ2,-1.0]])],"derivedFrom":subQ1}),1.0]])]});}
            var Q58;
            {var subQ0=sQuery(id+"F3.wireOp",EDGE,"E59.trimOffspring");var subQ1=sQuery(id+"F3.wireOp",EDGE,"E52.trimOffspring");var subQ2=makeQuery(id+"F3.imprint","INTERSECT",VERTEX,{"derivedFrom":[subQ1,subQ0]});Q58=makeQuery(id+"F3.imprint","IMPRINT",FACE,{"disambiguationData":[TD([[makeQuery(id+"F3.imprint","IMPRINT",EDGE,{"disambiguationData":[TD([[subQ2,-1.0]])],"derivedFrom":subQ1}),-1.0]])]});}
            var Q59;
            Q59=makeQuery(id+"F3.imprint","IMPRINT",FACE,{"disambiguationData":[TD([[makeQuery(id+"F3.imprint","IMPRINT",EDGE,{"derivedFrom":makeQuery(id+"F1.opExtrude","CAP_EDGE",EDGE,{"disambiguationData":[OSD([sQuery(id+"F0.wireOp",EDGE,"E8.1.0.0")])],"isStart":false})}),-1.0]])]});
            var Q60;
            Q60=makeQuery(id+"F3.imprint","IMPRINT",FACE,{"disambiguationData":[TD([[makeQuery(id+"F3.imprint","IMPRINT",EDGE,{"derivedFrom":makeQuery(id+"F1.opExtrude","CAP_EDGE",EDGE,{"disambiguationData":[OSD([sQuery(id+"F0.wireOp",EDGE,"E7")])],"isStart":false})}),-1.0]])]});
            var Q61;
            {var subQ0=sQuery(id+"F3.wireOp",EDGE,"E49.trimOffspring");var subQ1=sQuery(id+"F3.wireOp",EDGE,"E47.trimOffspring");var subQ2=makeQuery(id+"F3.imprint","INTERSECT",VERTEX,{"derivedFrom":[subQ1,subQ0]});Q61=makeQuery(id+"F3.imprint","IMPRINT",FACE,{"disambiguationData":[TD([[makeQuery(id+"F3.imprint","IMPRINT",EDGE,{"disambiguationData":[TD([[subQ2,-1.0]])],"derivedFrom":subQ1}),-1.0]])]});}
            var Q62;
            {var subQ0=sQuery(id+"F3.wireOp",EDGE,"E75");Q62=makeQuery(id+"F3.imprint","IMPRINT",FACE,{"disambiguationData":[TD([[makeQuery(id+"F3.imprint","IMPRINT",EDGE,{"derivedFrom":subQ0}),-1.0]])]});}
            var Q63;
            {var subQ0=sQuery(id+"F3.wireOp",EDGE,"E64.trimOffspring");var subQ1=sQuery(id+"F3.wireOp",EDGE,"E50.trimOffspring");var subQ2=makeQuery(id+"F3.imprint","INTERSECT",VERTEX,{"derivedFrom":[subQ1,subQ0]});Q63=makeQuery(id+"F3.imprint","IMPRINT",FACE,{"disambiguationData":[TD([[makeQuery(id+"F3.imprint","IMPRINT",EDGE,{"disambiguationData":[TD([[subQ2,1.0]])],"derivedFrom":subQ1}),-1.0]])]});}
            var Q64;
            {var subQ0=sQuery(id+"F3.wireOp",EDGE,"E64.trimOffspring");var subQ1=sQuery(id+"F3.wireOp",EDGE,"E49.trimOffspring");var subQ2=makeQuery(id+"F3.imprint","INTERSECT",VERTEX,{"derivedFrom":[subQ1,subQ0]});Q64=makeQuery(id+"F3.imprint","IMPRINT",FACE,{"disambiguationData":[TD([[makeQuery(id+"F3.imprint","IMPRINT",EDGE,{"disambiguationData":[TD([[subQ2,1.0]])],"derivedFrom":subQ1}),1.0]])]});}
            var Q65;
            Q65=makeQuery(id+"F3.imprint","IMPRINT",FACE,{"disambiguationData":[TD([[makeQuery(id+"F3.imprint","IMPRINT",EDGE,{"derivedFrom":makeQuery(id+"F1.opExtrude","CAP_EDGE",EDGE,{"disambiguationData":[OSD([sQuery(id+"F0.wireOp",EDGE,"E15")])],"isStart":false})}),-1.0]])]});
            var Q66;
            {var subQ0=sQuery(id+"F3.wireOp",EDGE,"E33.trimOffspring");var subQ1=sQuery(id+"F3.wireOp",EDGE,"E29.0.2.1");var subQ2=makeQuery(id+"F3.imprint","INTERSECT",VERTEX,{"derivedFrom":[subQ1,subQ0]});Q66=makeQuery(id+"F3.imprint","IMPRINT",FACE,{"disambiguationData":[TD([[makeQuery(id+"F3.imprint","IMPRINT",EDGE,{"disambiguationData":[TD([[subQ2,1.0]])],"derivedFrom":subQ1}),-1.0]])]});}
            var Q67;
            {var subQ0=sQuery(id+"F3.wireOp",EDGE,"E33.trimOffspring");var subQ1=sQuery(id+"F3.wireOp",EDGE,"E29.0.1.0");var subQ2=makeQuery(id+"F3.imprint","INTERSECT",VERTEX,{"derivedFrom":[subQ1,subQ0]});Q67=makeQuery(id+"F3.imprint","IMPRINT",FACE,{"disambiguationData":[TD([[makeQuery(id+"F3.imprint","IMPRINT",EDGE,{"disambiguationData":[TD([[subQ2,1.0]])],"derivedFrom":subQ1}),1.0]])]});}
            var Q68;
            {var subQ0=sQuery(id+"F3.wireOp",EDGE,"E28.1.0.0");var subQ1=sQuery(id+"F3.wireOp",EDGE,"E21.0");var subQ2=makeQuery(id+"F3.imprint","INTERSECT",VERTEX,{"derivedFrom":[subQ1,subQ0]});Q68=makeQuery(id+"F3.imprint","IMPRINT",FACE,{"disambiguationData":[TD([[makeQuery(id+"F3.imprint","IMPRINT",EDGE,{"disambiguationData":[TD([[subQ2,1.0]])],"derivedFrom":subQ1}),1.0]])]});}
            var Q69;
            {var subQ3=sQuery(id+"F3.wireOp",EDGE,"E21.11");Q69=makeQuery(id+"F3.imprint","IMPRINT",FACE,{"disambiguationData":[TD([[makeQuery(id+"F3.imprint","IMPRINT",EDGE,{"derivedFrom":subQ3}),-1.0]])]});}
            var Q70;
            {var subQ0=sQuery(id+"F3.wireOp",EDGE,"E26");var subQ1=sQuery(id+"F3.wireOp",EDGE,"E21.2");var subQ2=makeQuery(id+"F3.imprint","INTERSECT",VERTEX,{"derivedFrom":[subQ1,subQ0]});Q70=makeQuery(id+"F3.imprint","IMPRINT",FACE,{"disambiguationData":[TD([[makeQuery(id+"F3.imprint","IMPRINT",EDGE,{"disambiguationData":[TD([[subQ2,-1.0]])],"derivedFrom":subQ1}),-1.0]])]});}
            var Q71;
            {var subQ0=sQuery(id+"F3.wireOp",EDGE,"E28.2.0.0");var subQ1=sQuery(id+"F3.wireOp",EDGE,"E21.0");var subQ2=makeQuery(id+"F3.imprint","INTERSECT",VERTEX,{"derivedFrom":[subQ1,subQ0]});Q71=makeQuery(id+"F3.imprint","IMPRINT",FACE,{"disambiguationData":[TD([[makeQuery(id+"F3.imprint","IMPRINT",EDGE,{"disambiguationData":[TD([[subQ2,1.0]])],"derivedFrom":subQ1}),1.0]])]});}
            var Q72;
            {var subQ0=sQuery(id+"F3.wireOp",EDGE,"E22.right");Q72=makeQuery(id+"F3.imprint","IMPRINT",FACE,{"disambiguationData":[TD([[makeQuery(id+"F3.imprint","IMPRINT",EDGE,{"derivedFrom":subQ0}),1.0]])]});}
            var Q73;
            {var subQ0=sQuery(id+"F3.wireOp",EDGE,"E61.trimOffspring");var subQ1=sQuery(id+"F3.wireOp",EDGE,"E21.6");var subQ2=makeQuery(id+"F3.imprint","INTERSECT",VERTEX,{"derivedFrom":[subQ1,subQ0]});Q73=makeQuery(id+"F3.imprint","IMPRINT",FACE,{"disambiguationData":[TD([[makeQuery(id+"F3.imprint","IMPRINT",EDGE,{"disambiguationData":[TD([[subQ2,1.0]])],"derivedFrom":subQ1}),1.0]])]});}
            var Q74;
            {var subQ0=sQuery(id+"F3.wireOp",EDGE,"E68.trimOffspring");var subQ1=sQuery(id+"F3.wireOp",EDGE,"E21.4");var subQ2=makeQuery(id+"F3.imprint","INTERSECT",VERTEX,{"derivedFrom":[subQ1,subQ0]});Q74=makeQuery(id+"F3.imprint","IMPRINT",FACE,{"disambiguationData":[TD([[makeQuery(id+"F3.imprint","IMPRINT",EDGE,{"disambiguationData":[TD([[subQ2,1.0]])],"derivedFrom":subQ1}),-1.0]])]});}
            var Q75;
            {var subQ0=sQuery(id+"F3.wireOp",EDGE,"E70.trimOffspring");var subQ1=sQuery(id+"F3.wireOp",EDGE,"E21.4");var subQ2=makeQuery(id+"F3.imprint","INTERSECT",VERTEX,{"derivedFrom":[subQ1,subQ0]});Q75=makeQuery(id+"F3.imprint","IMPRINT",FACE,{"disambiguationData":[TD([[makeQuery(id+"F3.imprint","IMPRINT",EDGE,{"disambiguationData":[TD([[subQ2,-1.0]])],"derivedFrom":subQ1}),-1.0]])]});}
            var Q76;
            {var subQ0=sQuery(id+"F3.wireOp",EDGE,"E72.trimOffspring");var subQ1=sQuery(id+"F3.wireOp",EDGE,"E21.4");var subQ2=makeQuery(id+"F3.imprint","INTERSECT",VERTEX,{"derivedFrom":[subQ1,subQ0]});Q76=makeQuery(id+"F3.imprint","IMPRINT",FACE,{"disambiguationData":[TD([[makeQuery(id+"F3.imprint","IMPRINT",EDGE,{"disambiguationData":[TD([[subQ2,-1.0]])],"derivedFrom":subQ1}),-1.0]])]});}
            var Q77;
            {var subQ0=sQuery(id+"F3.wireOp",EDGE,"E73.trimOffspring");var subQ1=sQuery(id+"F3.wireOp",EDGE,"E21.4");var subQ2=makeQuery(id+"F3.imprint","INTERSECT",VERTEX,{"derivedFrom":[subQ1,subQ0]});Q77=makeQuery(id+"F3.imprint","IMPRINT",FACE,{"disambiguationData":[TD([[makeQuery(id+"F3.imprint","IMPRINT",EDGE,{"disambiguationData":[TD([[subQ2,-1.0]])],"derivedFrom":subQ1}),-1.0]])]});}
            var Q78;
            {var subQ0=sQuery(id+"F3.wireOp",EDGE,"E40.trimOffspring");var subQ1=sQuery(id+"F3.wireOp",EDGE,"E21.9");var subQ2=makeQuery(id+"F3.imprint","INTERSECT",VERTEX,{"derivedFrom":[subQ1,subQ0]});Q78=makeQuery(id+"F3.imprint","IMPRINT",FACE,{"disambiguationData":[TD([[makeQuery(id+"F3.imprint","IMPRINT",EDGE,{"disambiguationData":[TD([[subQ2,-1.0]])],"derivedFrom":subQ1}),-1.0]])]});}
            var Q79;
            {var subQ0=sQuery(id+"F3.wireOp",EDGE,"E56.trimOffspring");var subQ1=sQuery(id+"F3.wireOp",EDGE,"E21.13");var subQ2=makeQuery(id+"F3.imprint","INTERSECT",VERTEX,{"derivedFrom":[subQ1,subQ0]});Q79=makeQuery(id+"F3.imprint","IMPRINT",FACE,{"disambiguationData":[TD([[makeQuery(id+"F3.imprint","IMPRINT",EDGE,{"disambiguationData":[TD([[subQ2,1.0]])],"derivedFrom":subQ1}),-1.0]])]});}
            var Q80;
            {var subQ0=sQuery(id+"F3.wireOp",EDGE,"E63.trimOffspring");var subQ1=sQuery(id+"F3.wireOp",EDGE,"E21.17");var subQ2=makeQuery(id+"F3.imprint","INTERSECT",VERTEX,{"derivedFrom":[subQ1,subQ0]});Q80=makeQuery(id+"F3.imprint","IMPRINT",FACE,{"disambiguationData":[TD([[makeQuery(id+"F3.imprint","IMPRINT",EDGE,{"disambiguationData":[TD([[subQ2,-1.0]])],"derivedFrom":subQ1}),-1.0]])]});}
            var Q81;
            {var subQ0=sQuery(id+"F3.wireOp",EDGE,"E29.0.1.0");var subQ1=sQuery(id+"F3.wireOp",EDGE,"E21.2");var subQ2=makeQuery(id+"F3.imprint","INTERSECT",VERTEX,{"derivedFrom":[subQ1,subQ0]});Q81=makeQuery(id+"F3.imprint","IMPRINT",FACE,{"disambiguationData":[TD([[makeQuery(id+"F3.imprint","IMPRINT",EDGE,{"disambiguationData":[TD([[subQ2,1.0]])],"derivedFrom":subQ1}),-1.0]])]});}
            var Q82;
            {var subQ0=sQuery(id+"F3.wireOp",EDGE,"E58.trimOffspring");var subQ1=sQuery(id+"F3.wireOp",EDGE,"E21.6");var subQ2=makeQuery(id+"F3.imprint","INTERSECT",VERTEX,{"derivedFrom":[subQ1,subQ0]});Q82=makeQuery(id+"F3.imprint","IMPRINT",FACE,{"disambiguationData":[TD([[makeQuery(id+"F3.imprint","IMPRINT",EDGE,{"disambiguationData":[TD([[subQ2,1.0]])],"derivedFrom":subQ1}),1.0]])]});}
            var Q83;
            {var subQ5=sQuery(id+"F3.wireOp",EDGE,"E81.trimOffspring");Q83=makeQuery(id+"F3.imprint","IMPRINT",FACE,{"disambiguationData":[TD([[makeQuery(id+"F3.imprint","IMPRINT",EDGE,{"derivedFrom":subQ5}),-1.0]])]});}
            var Q84;
            {var subQ0=sQuery(id+"F3.wireOp",EDGE,"E28.3.0.0");var subQ1=sQuery(id+"F3.wireOp",EDGE,"E21.0");var subQ2=makeQuery(id+"F3.imprint","INTERSECT",VERTEX,{"derivedFrom":[subQ1,subQ0]});Q84=makeQuery(id+"F3.imprint","IMPRINT",FACE,{"disambiguationData":[TD([[makeQuery(id+"F3.imprint","IMPRINT",EDGE,{"disambiguationData":[TD([[subQ2,1.0]])],"derivedFrom":subQ1}),1.0]])]});}
            var Q85;
            {var subQ1=sQuery(id+"F3.wireOp",EDGE,"E21.0");var subQ5=sQuery(id+"F3.wireOp",EDGE,"E25.MirrorCS");var subQ6=makeQuery(id+"F3.imprint","INTERSECT",VERTEX,{"derivedFrom":[subQ1,subQ5]});Q85=makeQuery(id+"F3.imprint","IMPRINT",FACE,{"disambiguationData":[TD([[makeQuery(id+"F3.imprint","IMPRINT",EDGE,{"disambiguationData":[TD([[subQ6,1.0]])],"derivedFrom":subQ1}),1.0]])]});}
            var Q86;
            {var subQ0=sQuery(id+"F3.wireOp",EDGE,"E28.2.0.1");var subQ5=sQuery(id+"F3.wireOp",EDGE,"E21.0");var subQ6=makeQuery(id+"F3.imprint","INTERSECT",VERTEX,{"derivedFrom":[subQ5,subQ0]});Q86=makeQuery(id+"F3.imprint","IMPRINT",FACE,{"disambiguationData":[TD([[makeQuery(id+"F3.imprint","IMPRINT",EDGE,{"disambiguationData":[TD([[subQ6,1.0]])],"derivedFrom":subQ5}),1.0]])]});}
            var Q87;
            {var subQ7=sQuery(id+"F3.wireOp",EDGE,"E21.4");var subQ9=sQuery(id+"F3.wireOp",EDGE,"E73.trimOffspring");var subQ11=makeQuery(id+"F3.imprint","INTERSECT",VERTEX,{"derivedFrom":[subQ7,subQ9]});Q87=makeQuery(id+"F3.imprint","IMPRINT",FACE,{"disambiguationData":[TD([[makeQuery(id+"F3.imprint","IMPRINT",EDGE,{"disambiguationData":[TD([[subQ11,1.0]])],"derivedFrom":subQ7}),-1.0]])]});}
            var Q88;
            {var subQ7=sQuery(id+"F3.wireOp",EDGE,"E68.trimOffspring");var subQ9=sQuery(id+"F3.wireOp",EDGE,"E21.4");var subQ10=makeQuery(id+"F3.imprint","INTERSECT",VERTEX,{"derivedFrom":[subQ9,subQ7]});Q88=makeQuery(id+"F3.imprint","IMPRINT",FACE,{"disambiguationData":[TD([[makeQuery(id+"F3.imprint","IMPRINT",EDGE,{"disambiguationData":[TD([[subQ10,-1.0]])],"derivedFrom":subQ9}),-1.0]])]});}
            extrude(context, id + "F4", {"entities" : qUnion([Q0, Q1, Q2, Q3, Q4, Q5, Q6, Q7, Q8, Q9, Q10, Q11, Q12, Q13, Q14, Q15, Q16, Q17, Q18, Q19, Q20, Q21, Q22, Q23, Q24, Q25, Q26, Q27, Q28, Q29, Q30, Q31, Q32, Q33, Q34, Q35, Q36, Q37, Q38, Q39, Q40, Q41, Q42, Q43, Q44, Q45, Q46, Q47, Q48, Q49, Q50, Q51, Q52, Q53, Q54, Q55, Q56, Q57, Q58, Q59, Q60, Q61, Q62, Q63, Q64, Q65, Q66, Q67, Q68, Q69, Q70, Q71, Q72, Q73, Q74, Q75, Q76, Q77, Q78, Q79, Q80, Q81, Q82, Q83, Q84, Q85, Q86, Q87, Q88]), "operationType" : NewBodyOperationType.ADD, "depth" : 2 * mm});
        }
        {
            var Q0;
            Q0=makeQuery(id+"F4.opExtrude","SWEPT_EDGE",EDGE,{"disambiguationData":[OSD([sQuery(id+"F3.wireOp",EDGE,"E24"),sQuery(id+"F3.wireOp",EDGE,"E29.0.2.0")])]});
            var Q1;
            Q1=makeQuery(id+"F4.opExtrude","SWEPT_EDGE",EDGE,{"disambiguationData":[OSD([sQuery(id+"F3.wireOp",EDGE,"E25.MirrorCS"),sQuery(id+"F3.wireOp",EDGE,"E31.trimOffspring")])]});
            var Q2;
            Q2=makeQuery(id+"F4.opExtrude","SWEPT_EDGE",EDGE,{"disambiguationData":[OSD([sQuery(id+"F3.wireOp",EDGE,"E28.1.0.0"),sQuery(id+"F3.wireOp",EDGE,"E31.trimOffspring")])]});
            var Q3;
            Q3=makeQuery(id+"F4.opExtrude","SWEPT_EDGE",EDGE,{"disambiguationData":[OSD([sQuery(id+"F3.wireOp",EDGE,"E28.1.0.1"),sQuery(id+"F3.wireOp",EDGE,"E40.trimOffspring")])]});
            var Q4;
            Q4=makeQuery(id+"F4.opExtrude","SWEPT_EDGE",EDGE,{"disambiguationData":[OSD([sQuery(id+"F3.wireOp",EDGE,"E28.2.0.0"),sQuery(id+"F3.wireOp",EDGE,"E40.trimOffspring")])]});
            var Q5;
            Q5=makeQuery(id+"F4.opExtrude","SWEPT_EDGE",EDGE,{"disambiguationData":[OSD([sQuery(id+"F3.wireOp",EDGE,"E28.2.0.1"),sQuery(id+"F3.wireOp",EDGE,"E41.trimOffspring")])]});
            var Q6;
            Q6=makeQuery(id+"F4.opExtrude","SWEPT_EDGE",EDGE,{"disambiguationData":[OSD([sQuery(id+"F3.wireOp",EDGE,"E28.3.0.0"),sQuery(id+"F3.wireOp",EDGE,"E41.trimOffspring")])]});
            var Q7;
            Q7=makeQuery(id+"F4.opExtrude","SWEPT_EDGE",EDGE,{"disambiguationData":[OSD([sQuery(id+"F3.wireOp",EDGE,"E28.3.0.1"),sQuery(id+"F3.wireOp",EDGE,"E42.trimOffspring")])]});
            var Q8;
            Q8=makeQuery(id+"F4.opExtrude","SWEPT_EDGE",EDGE,{"disambiguationData":[OSD([sQuery(id+"F3.wireOp",EDGE,"E39.trimOffspring"),sQuery(id+"F3.wireOp",EDGE,"E58.trimOffspring")])]});
            var Q9;
            Q9=makeQuery(id+"F4.opExtrude","SWEPT_EDGE",EDGE,{"disambiguationData":[OSD([sQuery(id+"F3.wireOp",EDGE,"E38.trimOffspring"),sQuery(id+"F3.wireOp",EDGE,"E57.trimOffspring")])]});
            var Q10;
            Q10=makeQuery(id+"F4.opExtrude","SWEPT_EDGE",EDGE,{"disambiguationData":[OSD([sQuery(id+"F3.wireOp",EDGE,"E37.trimOffspring"),sQuery(id+"F3.wireOp",EDGE,"E57.trimOffspring")])]});
            var Q11;
            Q11=makeQuery(id+"F4.opExtrude","SWEPT_EDGE",EDGE,{"disambiguationData":[OSD([sQuery(id+"F3.wireOp",EDGE,"E36.trimOffspring"),sQuery(id+"F3.wireOp",EDGE,"E56.trimOffspring")])]});
            var Q12;
            Q12=makeQuery(id+"F4.opExtrude","SWEPT_EDGE",EDGE,{"disambiguationData":[OSD([sQuery(id+"F3.wireOp",EDGE,"E34.trimOffspring"),sQuery(id+"F3.wireOp",EDGE,"E46.trimOffspring")])]});
            var Q13;
            Q13=makeQuery(id+"F4.opExtrude","SWEPT_EDGE",EDGE,{"disambiguationData":[OSD([sQuery(id+"F3.wireOp",EDGE,"E35.trimOffspring"),sQuery(id+"F3.wireOp",EDGE,"E56.trimOffspring")])]});
            var Q14;
            Q14=makeQuery(id+"F4.opExtrude","SWEPT_EDGE",EDGE,{"disambiguationData":[OSD([sQuery(id+"F3.wireOp",EDGE,"E29.0.1.0"),sQuery(id+"F3.wireOp",EDGE,"E33.trimOffspring")])]});
            var Q15;
            Q15=makeQuery(id+"F4.opExtrude","SWEPT_EDGE",EDGE,{"disambiguationData":[OSD([sQuery(id+"F3.wireOp",EDGE,"E32.trimOffspring"),sQuery(id+"F3.wireOp",EDGE,"E46.trimOffspring")])]});
            var Q16;
            Q16=makeQuery(id+"F4.opExtrude","SWEPT_EDGE",EDGE,{"disambiguationData":[OSD([sQuery(id+"F3.wireOp",EDGE,"E29.0.1.1"),sQuery(id+"F3.wireOp",EDGE,"E48.trimOffspring")])]});
            var Q17;
            Q17=makeQuery(id+"F4.opExtrude","SWEPT_EDGE",EDGE,{"disambiguationData":[OSD([sQuery(id+"F3.wireOp",EDGE,"E27.MirrorCS"),sQuery(id+"F3.wireOp",EDGE,"E48.trimOffspring")])]});
            var Q18;
            Q18=makeQuery(id+"F4.opExtrude","SWEPT_EDGE",EDGE,{"disambiguationData":[OSD([sQuery(id+"F3.wireOp",EDGE,"E49.trimOffspring"),sQuery(id+"F3.wireOp",EDGE,"E64.trimOffspring")])]});
            var Q19;
            Q19=makeQuery(id+"F4.opExtrude","SWEPT_EDGE",EDGE,{"disambiguationData":[OSD([sQuery(id+"F3.wireOp",EDGE,"E50.trimOffspring"),sQuery(id+"F3.wireOp",EDGE,"E64.trimOffspring")])]});
            var Q20;
            Q20=makeQuery(id+"F4.opExtrude","SWEPT_EDGE",EDGE,{"disambiguationData":[OSD([sQuery(id+"F3.wireOp",EDGE,"E50.trimOffspring"),sQuery(id+"F3.wireOp",EDGE,"E75")])]});
            var Q21;
            Q21=makeQuery(id+"F4.opExtrude","SWEPT_EDGE",EDGE,{"disambiguationData":[OSD([sQuery(id+"F3.wireOp",EDGE,"E51.trimOffspring"),sQuery(id+"F3.wireOp",EDGE,"E63.trimOffspring")])]});
            var Q22;
            Q22=makeQuery(id+"F4.opExtrude","SWEPT_EDGE",EDGE,{"disambiguationData":[OSD([sQuery(id+"F3.wireOp",EDGE,"E52.trimOffspring"),sQuery(id+"F3.wireOp",EDGE,"E63.trimOffspring")])]});
            var Q23;
            Q23=makeQuery(id+"F4.opExtrude","SWEPT_EDGE",EDGE,{"disambiguationData":[OSD([sQuery(id+"F3.wireOp",EDGE,"E52.trimOffspring"),sQuery(id+"F3.wireOp",EDGE,"E59.trimOffspring")])]});
            var Q24;
            Q24=makeQuery(id+"F4.opExtrude","SWEPT_EDGE",EDGE,{"disambiguationData":[OSD([sQuery(id+"F3.wireOp",EDGE,"E53.trimOffspring"),sQuery(id+"F3.wireOp",EDGE,"E62.trimOffspring")])]});
            var Q25;
            Q25=makeQuery(id+"F4.opExtrude","SWEPT_EDGE",EDGE,{"disambiguationData":[OSD([sQuery(id+"F3.wireOp",EDGE,"E54.trimOffspring"),sQuery(id+"F3.wireOp",EDGE,"E62.trimOffspring")])]});
            var Q26;
            Q26=makeQuery(id+"F4.opExtrude","SWEPT_EDGE",EDGE,{"disambiguationData":[OSD([sQuery(id+"F3.wireOp",EDGE,"E55.trimOffspring"),sQuery(id+"F3.wireOp",EDGE,"E61.trimOffspring")])]});
            var Q27;
            Q27=makeQuery(id+"F4.opExtrude","SWEPT_EDGE",EDGE,{"disambiguationData":[OSD([sQuery(id+"F3.wireOp",EDGE,"E54.trimOffspring"),sQuery(id+"F3.wireOp",EDGE,"E78.trimOffspring")])]});
            var Q28;
            Q28=makeQuery(id+"F4.opExtrude","SWEPT_EDGE",EDGE,{"disambiguationData":[OSD([sQuery(id+"F3.wireOp",EDGE,"E68.trimOffspring"),sQuery(id+"F3.wireOp",EDGE,"E80.trimOffspring")])]});
            var Q29;
            Q29=makeQuery(id+"F4.opExtrude","SWEPT_EDGE",EDGE,{"disambiguationData":[OSD([sQuery(id+"F3.wireOp",EDGE,"E26"),sQuery(id+"F3.wireOp",EDGE,"E74.trimOffspring")])]});
            var Q30;
            Q30=makeQuery(id+"F4.opExtrude","SWEPT_EDGE",EDGE,{"disambiguationData":[OSD([sQuery(id+"F3.wireOp",EDGE,"E65.trimOffspring"),sQuery(id+"F3.wireOp",EDGE,"E73.trimOffspring")])]});
            var Q31;
            Q31=makeQuery(id+"F4.opExtrude","SWEPT_EDGE",EDGE,{"disambiguationData":[OSD([sQuery(id+"F3.wireOp",EDGE,"E76"),sQuery(id+"F3.wireOp",EDGE,"E77.trimOffspring")])]});
            var Q32;
            Q32=makeQuery(id+"F4.opExtrude","SWEPT_EDGE",EDGE,{"disambiguationData":[OSD([sQuery(id+"F3.wireOp",EDGE,"E66.trimOffspring"),sQuery(id+"F3.wireOp",EDGE,"E72.trimOffspring")])]});
            var Q33;
            Q33=makeQuery(id+"F4.opExtrude","SWEPT_EDGE",EDGE,{"disambiguationData":[OSD([sQuery(id+"F3.wireOp",EDGE,"E66.trimOffspring"),sQuery(id+"F3.wireOp",EDGE,"E71.trimOffspring")])]});
            var Q34;
            Q34=makeQuery(id+"F4.opExtrude","SWEPT_EDGE",EDGE,{"disambiguationData":[OSD([sQuery(id+"F3.wireOp",EDGE,"E70.trimOffspring"),sQuery(id+"F3.wireOp",EDGE,"E80.trimOffspring")])]});
            var Q35;
            Q35=makeQuery(id+"F4.opExtrude","SWEPT_EDGE",EDGE,{"disambiguationData":[OSD([sQuery(id+"F3.wireOp",EDGE,"E67.trimOffspring"),sQuery(id+"F3.wireOp",EDGE,"E69.trimOffspring")])]});
            var Q36;
            Q36=makeQuery(id+"F4.opExtrude","SWEPT_EDGE",EDGE,{"disambiguationData":[OSD([sQuery(id+"F3.wireOp",EDGE,"E55.trimOffspring"),sQuery(id+"F3.wireOp",EDGE,"E60.trimOffspring")])]});
            var Q37;
            Q37=makeQuery(id+"F4.opExtrude","SWEPT_EDGE",EDGE,{"disambiguationData":[OSD([sQuery(id+"F3.wireOp",EDGE,"E53.trimOffspring"),sQuery(id+"F3.wireOp",EDGE,"E78.trimOffspring")])]});
            var Q38;
            Q38=makeQuery(id+"F4.opExtrude","SWEPT_EDGE",EDGE,{"disambiguationData":[OSD([sQuery(id+"F3.wireOp",EDGE,"E51.trimOffspring"),sQuery(id+"F3.wireOp",EDGE,"E59.trimOffspring")])]});
            var Q39;
            Q39=makeQuery(id+"F4.opExtrude","SWEPT_EDGE",EDGE,{"disambiguationData":[OSD([sQuery(id+"F3.wireOp",EDGE,"E47.trimOffspring"),sQuery(id+"F3.wireOp",EDGE,"E49.trimOffspring")])]});
            var Q40;
            Q40=makeQuery(id+"F4.opExtrude","SWEPT_EDGE",EDGE,{"disambiguationData":[OSD([sQuery(id+"F3.wireOp",EDGE,"E37.trimOffspring"),sQuery(id+"F3.wireOp",EDGE,"E44.trimOffspring")])]});
            var Q41;
            Q41=makeQuery(id+"F4.opExtrude","SWEPT_EDGE",EDGE,{"disambiguationData":[OSD([sQuery(id+"F3.wireOp",EDGE,"E38.trimOffspring"),sQuery(id+"F3.wireOp",EDGE,"E44.trimOffspring")])]});
            var Q42;
            Q42=makeQuery(id+"F4.opExtrude","SWEPT_EDGE",EDGE,{"disambiguationData":[OSD([sQuery(id+"F3.wireOp",EDGE,"E39.trimOffspring"),sQuery(id+"F3.wireOp",EDGE,"E43.trimOffspring")])]});
            var Q43;
            Q43=makeQuery(id+"F4.opExtrude","SWEPT_EDGE",EDGE,{"disambiguationData":[OSD([sQuery(id+"F3.wireOp",EDGE,"E36.trimOffspring"),sQuery(id+"F3.wireOp",EDGE,"E45.trimOffspring")])]});
            var Q44;
            Q44=makeQuery(id+"F4.opExtrude","SWEPT_EDGE",EDGE,{"disambiguationData":[OSD([sQuery(id+"F3.wireOp",EDGE,"E29.0.2.1"),sQuery(id+"F3.wireOp",EDGE,"E33.trimOffspring")])]});
            var Q45;
            Q45=makeQuery(id+"F4.opExtrude","SWEPT_EDGE",EDGE,{"disambiguationData":[OSD([sQuery(id+"F3.wireOp",EDGE,"E30.trimOffspring"),sQuery(id+"F3.wireOp",EDGE,"E32.trimOffspring")])]});
            var Q46;
            Q46=makeQuery(id+"F4.opExtrude","SWEPT_EDGE",EDGE,{"disambiguationData":[OSD([sQuery(id+"F3.wireOp",EDGE,"E30.trimOffspring"),sQuery(id+"F3.wireOp",EDGE,"E34.trimOffspring")])]});
            var Q47;
            Q47=makeQuery(id+"F4.opExtrude","SWEPT_EDGE",EDGE,{"disambiguationData":[OSD([sQuery(id+"F3.wireOp",EDGE,"E35.trimOffspring"),sQuery(id+"F3.wireOp",EDGE,"E45.trimOffspring")])]});
            fillet(context, id + "F5", {"entities" : qUnion([Q0, Q1, Q2, Q3, Q4, Q5, Q6, Q7, Q8, Q9, Q10, Q11, Q12, Q13, Q14, Q15, Q16, Q17, Q18, Q19, Q20, Q21, Q22, Q23, Q24, Q25, Q26, Q27, Q28, Q29, Q30, Q31, Q32, Q33, Q34, Q35, Q36, Q37, Q38, Q39, Q40, Q41, Q42, Q43, Q44, Q45, Q46, Q47]), "radius" : 1 * mm, "tangentPropagation" : true, "conicFillet" : false});
        }
        {
            var Q0;
            Q0=makeQuery(id+"F4.opExtrude","CAP_FACE",FACE,{"disambiguationData":[OSD([sQuery(id+"F0.wireOp",EDGE,"E4.right"),sQuery(id+"F0.wireOp",EDGE,"E8.1.0.0"),sQuery(id+"F0.wireOp",EDGE,"E8.1.1.0"),sQuery(id+"F0.wireOp",EDGE,"E10.1.0.0"),sQuery(id+"F0.wireOp",EDGE,"E11.MirrorC"),sQuery(id+"F0.wireOp",EDGE,"E13"),sQuery(id+"F0.wireOp",EDGE,"E14"),sQuery(id+"F0.wireOp",EDGE,"E15"),sQuery(id+"F0.wireOp",EDGE,"E16.MirrorC"),sQuery(id+"F0.wireOp",EDGE,"E17.MirrorC"),sQuery(id+"F0.wireOp",EDGE,"E18.MirrorC"),sQuery(id+"F0.wireOp",EDGE,"E19.MirrorC"),sQuery(id+"F0.wireOp",EDGE,"E20.MirrorC"),sQuery(id+"F3.wireOp",EDGE,"E21.0"),sQuery(id+"F3.wireOp",EDGE,"E21.1"),sQuery(id+"F3.wireOp",EDGE,"E21.2"),sQuery(id+"F3.wireOp",EDGE,"E21.3"),sQuery(id+"F3.wireOp",EDGE,"E21.4"),sQuery(id+"F3.wireOp",EDGE,"E21.5"),sQuery(id+"F3.wireOp",EDGE,"E21.6"),sQuery(id+"F3.wireOp",EDGE,"E21.7"),sQuery(id+"F3.wireOp",EDGE,"E21.8"),sQuery(id+"F3.wireOp",EDGE,"E21.9"),sQuery(id+"F3.wireOp",EDGE,"E21.10"),sQuery(id+"F3.wireOp",EDGE,"E21.11"),sQuery(id+"F3.wireOp",EDGE,"E21.12"),sQuery(id+"F3.wireOp",EDGE,"E21.13"),sQuery(id+"F3.wireOp",EDGE,"E21.14"),sQuery(id+"F3.wireOp",EDGE,"E21.15"),sQuery(id+"F3.wireOp",EDGE,"E21.16"),sQuery(id+"F3.wireOp",EDGE,"E21.17"),sQuery(id+"F3.wireOp",EDGE,"E21.18"),sQuery(id+"F3.wireOp",EDGE,"E21.19"),sQuery(id+"F3.wireOp",EDGE,"E22.left"),sQuery(id+"F3.wireOp",EDGE,"E22.right"),sQuery(id+"F3.wireOp",EDGE,"E23.trimOffspring"),sQuery(id+"F3.wireOp",EDGE,"E24"),sQuery(id+"F3.wireOp",EDGE,"E25.MirrorCS"),sQuery(id+"F3.wireOp",EDGE,"E26"),sQuery(id+"F3.wireOp",EDGE,"E27.MirrorCS"),sQuery(id+"F3.wireOp",EDGE,"E28.1.0.0"),sQuery(id+"F3.wireOp",EDGE,"E28.1.0.1"),sQuery(id+"F3.wireOp",EDGE,"E28.2.0.0"),sQuery(id+"F3.wireOp",EDGE,"E28.2.0.1"),sQuery(id+"F3.wireOp",EDGE,"E28.3.0.0"),sQuery(id+"F3.wireOp",EDGE,"E28.3.0.1"),sQuery(id+"F3.wireOp",EDGE,"E29.0.1.0"),sQuery(id+"F3.wireOp",EDGE,"E29.0.1.1"),sQuery(id+"F3.wireOp",EDGE,"E29.0.2.0"),sQuery(id+"F3.wireOp",EDGE,"E29.0.2.1"),sQuery(id+"F3.wireOp",EDGE,"E31.trimOffspring"),sQuery(id+"F3.wireOp",EDGE,"E33.trimOffspring"),sQuery(id+"F3.wireOp",EDGE,"E35.trimOffspring"),sQuery(id+"F3.wireOp",EDGE,"E36.trimOffspring"),sQuery(id+"F3.wireOp",EDGE,"E39.trimOffspring"),sQuery(id+"F3.wireOp",EDGE,"E40.trimOffspring"),sQuery(id+"F3.wireOp",EDGE,"E41.trimOffspring"),sQuery(id+"F3.wireOp",EDGE,"E42.trimOffspring"),sQuery(id+"F3.wireOp",EDGE,"E43.trimOffspring"),sQuery(id+"F3.wireOp",EDGE,"E45.trimOffspring"),sQuery(id+"F3.wireOp",EDGE,"E48.trimOffspring"),sQuery(id+"F3.wireOp",EDGE,"E51.trimOffspring"),sQuery(id+"F3.wireOp",EDGE,"E52.trimOffspring"),sQuery(id+"F3.wireOp",EDGE,"E55.trimOffspring"),sQuery(id+"F3.wireOp",EDGE,"E56.trimOffspring"),sQuery(id+"F3.wireOp",EDGE,"E58.trimOffspring"),sQuery(id+"F3.wireOp",EDGE,"E59.trimOffspring"),sQuery(id+"F3.wireOp",EDGE,"E60.trimOffspring"),sQuery(id+"F3.wireOp",EDGE,"E61.trimOffspring"),sQuery(id+"F3.wireOp",EDGE,"E63.trimOffspring"),sQuery(id+"F3.wireOp",EDGE,"E65.trimOffspring"),sQuery(id+"F3.wireOp",EDGE,"E66.trimOffspring"),sQuery(id+"F3.wireOp",EDGE,"E67.trimOffspring"),sQuery(id+"F3.wireOp",EDGE,"E68.trimOffspring"),sQuery(id+"F3.wireOp",EDGE,"E69.trimOffspring"),sQuery(id+"F3.wireOp",EDGE,"E70.trimOffspring"),sQuery(id+"F3.wireOp",EDGE,"E71.trimOffspring"),sQuery(id+"F3.wireOp",EDGE,"E72.trimOffspring"),sQuery(id+"F3.wireOp",EDGE,"E73.trimOffspring"),sQuery(id+"F3.wireOp",EDGE,"E74.trimOffspring"),sQuery(id+"F3.wireOp",EDGE,"E76"),sQuery(id+"F3.wireOp",EDGE,"E77.trimOffspring"),sQuery(id+"F3.wireOp",EDGE,"E80.trimOffspring"),sQuery(id+"F3.wireOp",EDGE,"E81.trimOffspring")])],"isStart":false});
            var sketch = newSketch(context, id + "F6", { "sketchPlane" : qUnion([Q0]) });
            skLineSegment(sketch, "E84.0", {"start": v(70.8, -11.4) * mm, "end": v(-11.4, -11.4) * mm, "construction": true});
            skLineSegment(sketch, "E85.0", {"start": v(9.9, 0) * mm, "end": v(9.9, -11.4) * mm, "construction": true});
            skLineSegment(sketch, "E86.bottom", {"start": v(11.4, -10.15) * mm, "end": v(8.4, -10.15) * mm});
            skLineSegment(sketch, "E86.top", {"start": v(11.4, -9.05) * mm, "end": v(8.4, -9.05) * mm});
            skLineSegment(sketch, "E86.left", {"start": v(11.4, -10.15) * mm, "end": v(11.4, -9.05) * mm});
            skLineSegment(sketch, "E86.right", {"start": v(8.4, -10.15) * mm, "end": v(8.4, -9.05) * mm});
            skPoint(sketch, "E86.middle", {"position": v(9.9, -9.6) * mm});
            skLineSegment(sketch, "E87.bottom", {"start": v(11.4, -7.55) * mm, "end": v(8.4, -7.55) * mm});
            skLineSegment(sketch, "E87.top", {"start": v(11.4, -6.45) * mm, "end": v(8.4, -6.45) * mm});
            skLineSegment(sketch, "E87.left", {"start": v(11.4, -7.55) * mm, "end": v(11.4, -6.45) * mm});
            skLineSegment(sketch, "E87.right", {"start": v(8.4, -7.55) * mm, "end": v(8.4, -6.45) * mm});
            skPoint(sketch, "E87.middle", {"position": v(9.9, -7) * mm});
            skLineSegment(sketch, "E88.MirrorCS", {"start": v(11.4, 46.05) * mm, "end": v(8.4, 46.05) * mm});
            skLineSegment(sketch, "E89.MirrorCS", {"start": v(8.4, 47.15) * mm, "end": v(8.4, 46.05) * mm});
            skLineSegment(sketch, "E90.MirrorCS", {"start": v(11.4, 47.15) * mm, "end": v(8.4, 47.15) * mm});
            skLineSegment(sketch, "E91.MirrorCS", {"start": v(11.4, 47.15) * mm, "end": v(11.4, 46.05) * mm});
            skLineSegment(sketch, "E92.MirrorCS", {"start": v(11.4, 48.65) * mm, "end": v(8.4, 48.65) * mm});
            skLineSegment(sketch, "E93.MirrorCS", {"start": v(8.4, 49.75) * mm, "end": v(8.4, 48.65) * mm});
            skLineSegment(sketch, "E94.MirrorCS", {"start": v(11.4, 49.75) * mm, "end": v(8.4, 49.75) * mm});
            skLineSegment(sketch, "E95.MirrorCS", {"start": v(11.4, 49.75) * mm, "end": v(11.4, 48.65) * mm});
            skLineSegment(sketch, "E96.MirrorCS", {"start": v(48, 49.75) * mm, "end": v(51, 49.75) * mm});
            skLineSegment(sketch, "E97.MirrorCS", {"start": v(51, 49.75) * mm, "end": v(51, 48.65) * mm});
            skLineSegment(sketch, "E98.MirrorCS", {"start": v(48, 48.65) * mm, "end": v(51, 48.65) * mm});
            skLineSegment(sketch, "E99.MirrorCS", {"start": v(48, 49.75) * mm, "end": v(48, 48.65) * mm});
            skLineSegment(sketch, "E100.MirrorCS", {"start": v(48, 47.15) * mm, "end": v(51, 47.15) * mm});
            skLineSegment(sketch, "E101.MirrorCS", {"start": v(51, 47.15) * mm, "end": v(51, 46.05) * mm});
            skLineSegment(sketch, "E102.MirrorCS", {"start": v(48, 47.15) * mm, "end": v(48, 46.05) * mm});
            skLineSegment(sketch, "E103.MirrorCS", {"start": v(48, 46.05) * mm, "end": v(51, 46.05) * mm});
            skLineSegment(sketch, "E104.MirrorCS", {"start": v(48, -6.45) * mm, "end": v(51, -6.45) * mm});
            skLineSegment(sketch, "E105.MirrorCS", {"start": v(51, -7.55) * mm, "end": v(51, -6.45) * mm});
            skLineSegment(sketch, "E106.MirrorCS", {"start": v(48, -7.55) * mm, "end": v(51, -7.55) * mm});
            skLineSegment(sketch, "E107.MirrorCS", {"start": v(48, -7.55) * mm, "end": v(48, -6.45) * mm});
            skLineSegment(sketch, "E108.MirrorCS", {"start": v(48, -9.05) * mm, "end": v(51, -9.05) * mm});
            skLineSegment(sketch, "E109.MirrorCS", {"start": v(51, -10.15) * mm, "end": v(51, -9.05) * mm});
            skLineSegment(sketch, "E110.MirrorCS", {"start": v(48, -10.15) * mm, "end": v(51, -10.15) * mm});
            skLineSegment(sketch, "E111.MirrorCS", {"start": v(48, -10.15) * mm, "end": v(48, -9.05) * mm});
            skSolve(sketch);
        }
        {
            var Q0;
            Q0 = qSketchRegion(id + "F6", true);
            extrude(context, id + "F7", {"entities" : qUnion([Q0]), "operationType" : NewBodyOperationType.REMOVE, "endBound" : BoundingType.THROUGH_ALL, "oppositeDirection" : true, "depth" : 25 * mm});
        }
    });
